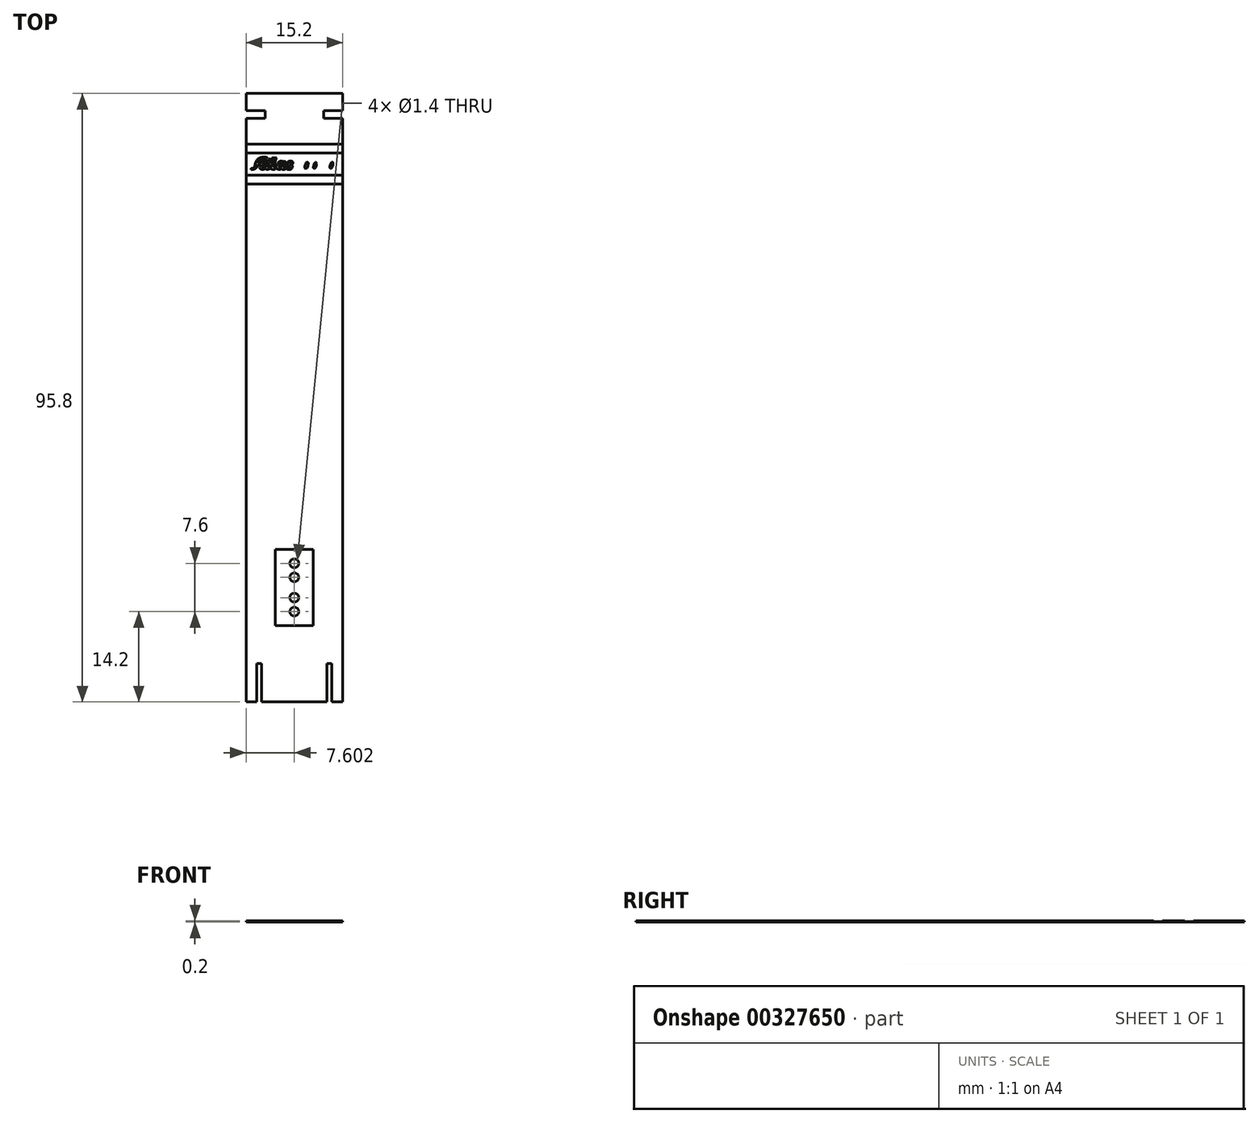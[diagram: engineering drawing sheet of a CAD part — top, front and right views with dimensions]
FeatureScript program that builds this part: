
annotation { "Feature Type Name" : "Feature", "Feature Type Description" : "" }
export const myFeature = defineFeature(function(context is Context, id is Id, definition is map)
    precondition{}
    {
        {
            var Q0;
            Q0=qCreatedBy(makeId("Top.planeOp"),FACE);
            var sketch = newSketch(context, id + "F0", { "sketchPlane" : qUnion([Q0])});
            skLineSegment(sketch, "E0.bottom", {"start": v(-50.14, 64.87) * mm, "end": v(-34.94, 64.87) * mm});
            skLineSegment(sketch, "E0.top", {"start": v(-50.14, -30.93) * mm, "end": v(-34.94, -30.93) * mm});
            skLineSegment(sketch, "E0.left", {"start": v(-50.14, 64.87) * mm, "end": v(-50.14, -30.93) * mm});
            skLineSegment(sketch, "E0.right", {"start": v(-34.94, 64.87) * mm, "end": v(-34.94, -30.93) * mm});
            skSolve(sketch);
        }
        {
            var Q0;
            Q0=makeQuery(id+"F0.imprint","IMPRINT",FACE,{"disambiguationData":[TD([[makeQuery(id+"F0.imprint","IMPRINT",EDGE,{"derivedFrom":sQuery(id+"F0.wireOp",EDGE,"E0.bottom")}),-1.0]])]});
            extrude(context, id + "F1", {"entities" : qUnion([Q0]), "depth" : 0.2 * mm});
        }
        {
            var Q0;
            Q0=makeQuery(id+"F1.opExtrude","CAP_FACE",FACE,{"disambiguationData":[OSD([sQuery(id+"F0.wireOp",EDGE,"E0.bottom"),sQuery(id+"F0.wireOp",EDGE,"E0.top"),sQuery(id+"F0.wireOp",EDGE,"E0.left"),sQuery(id+"F0.wireOp",EDGE,"E0.right")])],"isStart":false});
            var sketch = newSketch(context, id + "F2", { "sketchPlane" : qUnion([Q0])});
            skLineSegment(sketch, "E1.bottom", {"start": v(-50.14, 62.17) * mm, "end": v(-47.44, 62.17) * mm});
            skLineSegment(sketch, "E1.top", {"start": v(-50.14, 60.92) * mm, "end": v(-47.44, 60.92) * mm});
            skLineSegment(sketch, "E1.left", {"start": v(-50.14, 62.17) * mm, "end": v(-50.14, 60.92) * mm});
            skLineSegment(sketch, "E1.right", {"start": v(-47.14, 61.87) * mm, "end": v(-47.14, 61.22) * mm});
            skLineSegment(sketch, "E2.bottom", {"start": v(-34.94, 62.17) * mm, "end": v(-37.64, 62.17) * mm});
            skLineSegment(sketch, "E2.top", {"start": v(-34.94, 60.92) * mm, "end": v(-37.64, 60.92) * mm});
            skLineSegment(sketch, "E2.left", {"start": v(-34.94, 62.17) * mm, "end": v(-34.94, 60.92) * mm});
            skLineSegment(sketch, "E2.right", {"start": v(-37.94, 61.87) * mm, "end": v(-37.94, 61.22) * mm});
            skPoint(sketch, "E3.visualSharp", {"position": v(-37.94, 60.92) * mm});
            skPoint(sketch, "E4.visualSharp", {"position": v(-37.94, 62.17) * mm});
            skPoint(sketch, "E5.visualSharp", {"position": v(-47.14, 60.92) * mm});
            skPoint(sketch, "E6.visualSharp", {"position": v(-47.14, 62.17) * mm});
            skLineSegment(sketch, "E7", {"start": v(-37.94, 61.22) * mm, "end": v(-37.94, 60.92) * mm});
            skLineSegment(sketch, "E8", {"start": v(-37.64, 60.92) * mm, "end": v(-37.94, 60.92) * mm});
            skLineSegment(sketch, "E9", {"start": v(-37.94, 61.87) * mm, "end": v(-37.94, 62.17) * mm});
            skLineSegment(sketch, "E10", {"start": v(-37.64, 62.17) * mm, "end": v(-37.94, 62.17) * mm});
            skLineSegment(sketch, "E11", {"start": v(-47.44, 60.92) * mm, "end": v(-47.14, 60.92) * mm});
            skLineSegment(sketch, "E12", {"start": v(-47.14, 60.92) * mm, "end": v(-47.14, 61.22) * mm});
            skLineSegment(sketch, "E13", {"start": v(-47.14, 61.87) * mm, "end": v(-47.14, 62.17) * mm});
            skLineSegment(sketch, "E14", {"start": v(-47.14, 62.17) * mm, "end": v(-47.44, 62.17) * mm});
            skSolve(sketch);
        }
        {
            var Q0;
            Q0 = qSketchRegion(id + "F2", true);
            extrude(context, id + "F3", {"entities" : qUnion([Q0]), "operationType" : NewBodyOperationType.REMOVE, "oppositeDirection" : true, "depth" : 0.2 * mm});
        }
        {
            var Q0;
            Q0=makeQuery(id+"F1.opExtrude","CAP_FACE",FACE,{"disambiguationData":[OSD([sQuery(id+"F0.wireOp",EDGE,"E0.bottom"),sQuery(id+"F0.wireOp",EDGE,"E0.top"),sQuery(id+"F0.wireOp",EDGE,"E0.left"),sQuery(id+"F0.wireOp",EDGE,"E0.right")])],"isStart":false});
            var sketch = newSketch(context, id + "F4", { "sketchPlane" : qUnion([Q0])});
            skLineSegment(sketch, "E15", {"start": v(-48.26, 53.74) * mm, "end": v(-47.84, 53.74) * mm});
            skLineSegment(sketch, "E16", {"start": v(-47.84, 53.74) * mm, "end": v(-47.98, 53.3) * mm});
            skFitSpline(sketch, "E17", {"points": [v(-47.98, 53.3) * mm, v(-47.98, 53.14) * mm, v(-47.95, 53.02) * mm, v(-47.9, 52.98) * mm, v(-47.83, 52.94) * mm, v(-47.76, 52.92) * mm, v(-47.67, 52.9) * mm, v(-47.54, 52.88) * mm, v(-47.42, 52.9) * mm, v(-47.34, 52.94) * mm, v(-47.26, 52.97) * mm, v(-47.2, 53.02) * mm, v(-47.13, 53.08) * mm, v(-47.1, 53.12) * mm, v(-47.06, 53.12) * mm, v(-47.05, 53.07) * mm, v(-47, 52.97) * mm, v(-46.96, 52.94) * mm, v(-46.9, 52.9) * mm, v(-46.79, 52.88) * mm, v(-46.69, 52.88) * mm, v(-46.63, 52.9) * mm, v(-46.53, 52.93) * mm, v(-46.43, 52.98) * mm, v(-46.34, 53.03) * mm, v(-46.29, 53.06) * mm, v(-46.27, 53.1) * mm, v(-46.23, 53.1) * mm, v(-46.19, 53.13) * mm, v(-46.16, 53.06) * mm, v(-46.15, 53) * mm, v(-46.11, 52.95) * mm, v(-46.08, 52.92) * mm, v(-46, 52.9) * mm, v(-45.94, 52.87) * mm, v(-45.87, 52.89) * mm, v(-45.77, 52.89) * mm, v(-45.73, 52.91) * mm, v(-45.66, 52.93) * mm, v(-45.62, 52.95) * mm, v(-45.6, 52.97) * mm, v(-45.56, 53) * mm, v(-45.5, 53.03) * mm, v(-45.46, 53.09) * mm, v(-45.4, 53.13) * mm, v(-45.4, 53.18) * mm, v(-45.35, 53.2) * mm, v(-45.31, 53.2) * mm, v(-45.32, 53.15) * mm, v(-45.3, 53.1) * mm, v(-45.3, 53.08) * mm, v(-45.26, 53.04) * mm, v(-45.2, 52.98) * mm, v(-45.18, 52.95) * mm, v(-45.13, 52.91) * mm, v(-45.04, 52.88) * mm, v(-44.97, 52.87) * mm], "startDerivative": vector(-0.3, -5.65) * mm, "endDerivative": vector(3.86, 0.76) * mm});
            skFitSpline(sketch, "E18", {"points": [v(-44.97, 52.87) * mm, v(-44.9, 52.87) * mm, v(-44.85, 52.89) * mm, v(-44.81, 52.9) * mm, v(-44.77, 52.9) * mm, v(-44.73, 52.91) * mm, v(-44.72, 52.93) * mm, v(-44.68, 52.95) * mm, v(-44.67, 52.96) * mm, v(-44.64, 52.98) * mm, v(-44.6, 53) * mm, v(-44.6, 53.02) * mm, v(-44.57, 53.04) * mm, v(-44.55, 53.05) * mm, v(-44.53, 53.03) * mm, v(-44.5, 53) * mm, v(-44.48, 52.97) * mm, v(-44.46, 52.94) * mm, v(-44.44, 52.92) * mm, v(-44.42, 52.91) * mm, v(-44.4, 52.9) * mm, v(-44.36, 52.9) * mm, v(-44.33, 52.9) * mm, v(-44.28, 52.9) * mm, v(-44.24, 52.9) * mm, v(-44.21, 52.9) * mm, v(-44.18, 52.9) * mm, v(-44.16, 52.9) * mm, v(-44.12, 52.91) * mm, v(-44.08, 52.93) * mm, v(-44.03, 52.95) * mm, v(-44.02, 52.97) * mm, v(-44, 52.98) * mm, v(-43.97, 53) * mm, v(-43.94, 53.02) * mm, v(-43.92, 53.03) * mm, v(-43.89, 53.06) * mm, v(-43.87, 53.08) * mm, v(-43.85, 53.1) * mm, v(-43.83, 53.07) * mm, v(-43.81, 53.05) * mm, v(-43.78, 53) * mm, v(-43.76, 53) * mm, v(-43.75, 52.98) * mm, v(-43.72, 52.95) * mm, v(-43.7, 52.94) * mm, v(-43.67, 52.92) * mm, v(-43.65, 52.91) * mm, v(-43.64, 52.9) * mm, v(-43.59, 52.89) * mm, v(-43.55, 52.87) * mm, v(-43.53, 52.87) * mm, v(-43.5, 52.87) * mm, v(-43.47, 52.87) * mm, v(-43.43, 52.87) * mm, v(-43.39, 52.87) * mm, v(-43.35, 52.87) * mm, v(-43.3, 52.87) * mm, v(-43.25, 52.87) * mm, v(-43.22, 52.89) * mm, v(-43.2, 52.9) * mm, v(-43.15, 52.92) * mm, v(-43.1, 52.94) * mm, v(-43.07, 52.96) * mm, v(-43.05, 52.97) * mm, v(-43, 53) * mm, v(-42.97, 53.02) * mm, v(-42.94, 53.06) * mm, v(-42.9, 53.1) * mm, v(-42.9, 53.1) * mm, v(-42.87, 53.16) * mm, v(-42.85, 53.19) * mm], "startDerivative": vector(3.83, -0.43) * mm, "endDerivative": vector(1.39, 4.88) * mm});
            skFitSpline(sketch, "E19", {"points": [v(-42.85, 53.19) * mm, v(-42.84, 53.23) * mm, v(-42.83, 53.27) * mm, v(-42.82, 53.3) * mm, v(-42.83, 53.33) * mm, v(-42.83, 53.36) * mm, v(-42.83, 53.4) * mm, v(-42.83, 53.42) * mm, v(-42.85, 53.45) * mm, v(-42.85, 53.46) * mm, v(-42.86, 53.5) * mm, v(-42.89, 53.52) * mm, v(-42.92, 53.55) * mm, v(-42.96, 53.59) * mm, v(-43, 53.61) * mm, v(-43.02, 53.62) * mm, v(-43.05, 53.64) * mm, v(-43.08, 53.66) * mm, v(-43.12, 53.68) * mm, v(-43.14, 53.7) * mm, v(-43.15, 53.71) * mm, v(-43.2, 53.75) * mm, v(-43.2, 53.76) * mm, v(-43.22, 53.78) * mm, v(-43.24, 53.82) * mm, v(-43.25, 53.85) * mm, v(-43.26, 53.87) * mm, v(-43.27, 53.9) * mm, v(-43.27, 53.94) * mm, v(-43.26, 53.96) * mm, v(-43.25, 53.98) * mm, v(-43.23, 54) * mm, v(-43.21, 54.01) * mm, v(-43.2, 54.03) * mm, v(-43.17, 54.03) * mm, v(-43.15, 54.04) * mm, v(-43.13, 54.04) * mm, v(-43.1, 54.04) * mm, v(-43.08, 54.04) * mm, v(-43.07, 54.02) * mm, v(-43.07, 54) * mm, v(-43.07, 53.99) * mm, v(-43.07, 53.97) * mm, v(-43.07, 53.96) * mm, v(-43.08, 53.95) * mm, v(-43.08, 53.92) * mm, v(-43.08, 53.9) * mm, v(-43.08, 53.87) * mm, v(-43.08, 53.86) * mm, v(-43.07, 53.85) * mm, v(-43.06, 53.82) * mm, v(-43.05, 53.81) * mm, v(-43.03, 53.8) * mm, v(-43.02, 53.78) * mm, v(-43, 53.78) * mm, v(-43, 53.77) * mm, v(-42.97, 53.75) * mm, v(-42.96, 53.75) * mm, v(-42.93, 53.75) * mm, v(-42.9, 53.74) * mm, v(-42.85, 53.75) * mm, v(-42.81, 53.77) * mm, v(-42.8, 53.78) * mm, v(-42.79, 53.79) * mm, v(-42.78, 53.8) * mm, v(-42.76, 53.82) * mm, v(-42.75, 53.83) * mm, v(-42.75, 53.86) * mm, v(-42.75, 53.88) * mm], "startDerivative": vector(0.54, 2.4) * mm, "endDerivative": vector(0.03, 1.76) * mm});
            skFitSpline(sketch, "E20", {"points": [v(-42.75, 53.88) * mm, v(-42.74, 53.91) * mm, v(-42.74, 53.92) * mm, v(-42.74, 53.95) * mm, v(-42.75, 53.96) * mm, v(-42.75, 53.99) * mm, v(-42.76, 54) * mm, v(-42.76, 54.02) * mm, v(-42.77, 54.03) * mm, v(-42.77, 54.04) * mm, v(-42.78, 54.06) * mm, v(-42.8, 54.08) * mm, v(-42.8, 54.08) * mm, v(-42.8, 54.1) * mm, v(-42.81, 54.1) * mm, v(-42.81, 54.11) * mm, v(-42.83, 54.12) * mm, v(-42.84, 54.13) * mm, v(-42.85, 54.14) * mm, v(-42.86, 54.15) * mm, v(-42.87, 54.15) * mm], "startDerivative": vector(0.19, 0.47) * mm, "endDerivative": vector(-0.08, 0.05) * mm});
            skFitSpline(sketch, "E21", {"points": [v(-42.87, 54.15) * mm, v(-42.9, 54.17) * mm, v(-42.91, 54.18) * mm, v(-42.95, 54.19) * mm, v(-42.97, 54.2) * mm, v(-42.98, 54.2) * mm, v(-43.02, 54.21) * mm, v(-43.05, 54.22) * mm, v(-43.1, 54.22) * mm, v(-43.17, 54.22) * mm, v(-43.2, 54.22) * mm, v(-43.21, 54.22) * mm, v(-43.23, 54.22) * mm, v(-43.26, 54.22) * mm, v(-43.3, 54.22) * mm, v(-43.31, 54.21) * mm, v(-43.34, 54.21) * mm, v(-43.37, 54.2) * mm, v(-43.39, 54.2) * mm, v(-43.4, 54.18) * mm, v(-43.43, 54.17) * mm, v(-43.45, 54.16) * mm, v(-43.53, 54.1) * mm, v(-43.56, 54.08) * mm, v(-43.58, 54.06) * mm, v(-43.59, 54.05) * mm, v(-43.6, 54.03) * mm, v(-43.63, 54) * mm, v(-43.64, 53.97) * mm, v(-43.65, 53.93) * mm, v(-43.66, 53.91) * mm, v(-43.68, 53.87) * mm, v(-43.68, 53.83) * mm, v(-43.68, 53.8) * mm, v(-43.67, 53.76) * mm, v(-43.67, 53.72) * mm, v(-43.67, 53.7) * mm, v(-43.66, 53.67) * mm, v(-43.65, 53.64) * mm, v(-43.62, 53.62) * mm, v(-43.6, 53.6) * mm, v(-43.58, 53.57) * mm, v(-43.56, 53.55) * mm, v(-43.53, 53.54) * mm, v(-43.5, 53.52) * mm, v(-43.48, 53.5) * mm, v(-43.46, 53.48) * mm, v(-43.42, 53.45) * mm, v(-43.4, 53.43) * mm, v(-43.35, 53.4) * mm, v(-43.32, 53.38) * mm, v(-43.29, 53.35) * mm, v(-43.27, 53.33) * mm, v(-43.25, 53.29) * mm, v(-43.23, 53.24) * mm, v(-43.23, 53.2) * mm, v(-43.24, 53.17) * mm, v(-43.27, 53.12) * mm, v(-43.3, 53.1) * mm, v(-43.34, 53.07) * mm, v(-43.43, 53.05) * mm, v(-43.46, 53.05) * mm, v(-43.48, 53.05) * mm, v(-43.5, 53.05) * mm, v(-43.53, 53.06) * mm, v(-43.55, 53.06) * mm, v(-43.56, 53.06) * mm, v(-43.6, 53.07) * mm, v(-43.61, 53.1) * mm, v(-43.62, 53.1) * mm, v(-43.64, 53.13) * mm, v(-43.65, 53.15) * mm, v(-43.65, 53.16) * mm, v(-43.66, 53.2) * mm, v(-43.64, 53.2) * mm, v(-43.6, 53.2) * mm, v(-43.59, 53.22) * mm, v(-43.58, 53.23) * mm, v(-43.56, 53.25) * mm, v(-43.56, 53.26) * mm, v(-43.56, 53.27) * mm, v(-43.56, 53.3) * mm, v(-43.56, 53.31) * mm, v(-43.56, 53.34) * mm, v(-43.56, 53.38) * mm, v(-43.56, 53.4) * mm, v(-43.57, 53.42) * mm, v(-43.6, 53.43) * mm, v(-43.6, 53.45) * mm, v(-43.63, 53.46) * mm, v(-43.7, 53.48) * mm, v(-43.73, 53.49) * mm], "startDerivative": vector(-2.33, 2.26) * mm, "endDerivative": vector(-4.26, -1.5) * mm});
            skFitSpline(sketch, "E22", {"points": [v(-43.73, 53.49) * mm, v(-43.77, 53.49) * mm, v(-43.79, 53.47) * mm, v(-43.81, 53.45) * mm, v(-43.83, 53.44) * mm, v(-43.85, 53.43) * mm, v(-43.86, 53.41) * mm, v(-43.87, 53.4) * mm, v(-43.87, 53.39) * mm, v(-43.88, 53.37) * mm, v(-43.88, 53.35) * mm, v(-43.88, 53.33) * mm, v(-43.88, 53.31) * mm, v(-43.88, 53.3) * mm, v(-43.88, 53.28) * mm, v(-43.89, 53.26) * mm, v(-43.9, 53.25) * mm, v(-43.92, 53.23) * mm, v(-43.94, 53.22) * mm, v(-43.95, 53.2) * mm, v(-43.97, 53.18) * mm, v(-43.98, 53.18) * mm, v(-44, 53.18) * mm, v(-44.04, 53.18) * mm, v(-44.08, 53.18) * mm, v(-44.1, 53.19) * mm, v(-44.12, 53.2) * mm, v(-44.13, 53.2) * mm, v(-44.14, 53.23) * mm, v(-44.14, 53.25) * mm, v(-44.14, 53.27) * mm, v(-44.13, 53.31) * mm, v(-44.13, 53.34) * mm, v(-44.13, 53.36) * mm, v(-44.12, 53.38) * mm, v(-44.12, 53.4) * mm, v(-44.11, 53.42) * mm, v(-44.1, 53.47) * mm, v(-44.1, 53.5) * mm, v(-44.1, 53.52) * mm, v(-44.09, 53.54) * mm, v(-44.08, 53.56) * mm, v(-44.08, 53.58) * mm, v(-44.07, 53.6) * mm, v(-44.06, 53.62) * mm, v(-44.06, 53.66) * mm, v(-44.05, 53.68) * mm, v(-44.05, 53.71) * mm, v(-44.04, 53.74) * mm, v(-44.04, 53.75) * mm, v(-44.02, 53.87) * mm, v(-44, 53.97) * mm, v(-43.98, 54.01) * mm, v(-43.96, 54.05) * mm, v(-43.96, 54.08) * mm, v(-43.94, 54.1) * mm, v(-43.94, 54.15) * mm, v(-43.94, 54.17) * mm, v(-43.94, 54.18) * mm, v(-43.96, 54.17) * mm, v(-44.04, 54.17) * mm, v(-44.09, 54.18) * mm, v(-44.12, 54.18) * mm, v(-44.16, 54.17) * mm, v(-44.2, 54.18) * mm, v(-44.26, 54.18) * mm, v(-44.3, 54.18) * mm, v(-44.31, 54.12) * mm, v(-44.33, 54.1) * mm, v(-44.38, 54.11) * mm, v(-44.4, 54.13) * mm, v(-44.4, 54.15) * mm, v(-44.44, 54.18) * mm, v(-44.46, 54.18) * mm, v(-44.5, 54.2) * mm, v(-44.53, 54.2) * mm, v(-44.59, 54.2) * mm, v(-44.64, 54.21) * mm, v(-44.7, 54.21) * mm, v(-44.72, 54.21) * mm, v(-44.76, 54.2) * mm, v(-44.82, 54.2) * mm, v(-44.82, 54.17) * mm, v(-44.85, 54.16) * mm, v(-44.88, 54.14) * mm, v(-44.9, 54.12) * mm, v(-44.94, 54.1) * mm, v(-44.97, 54.08) * mm, v(-44.99, 54.06) * mm, v(-45, 54.04) * mm, v(-45.02, 54.01) * mm], "startDerivative": vector(-3.3, 0.4) * mm, "endDerivative": vector(-1.45, -2.51) * mm});
            skFitSpline(sketch, "E23", {"points": [v(-45.02, 54.01) * mm, v(-45.08, 53.94) * mm, v(-45.13, 53.87) * mm, v(-45.16, 53.83) * mm, v(-45.22, 53.73) * mm, v(-45.26, 53.67) * mm, v(-45.28, 53.64) * mm, v(-45.3, 53.59) * mm, v(-45.32, 53.56) * mm, v(-45.35, 53.52) * mm, v(-45.36, 53.49) * mm, v(-45.38, 53.45) * mm, v(-45.4, 53.43) * mm, v(-45.44, 53.37) * mm, v(-45.46, 53.34) * mm, v(-45.47, 53.33) * mm, v(-45.5, 53.3) * mm, v(-45.51, 53.29) * mm, v(-45.53, 53.26) * mm, v(-45.55, 53.23) * mm, v(-45.57, 53.22) * mm, v(-45.58, 53.2) * mm, v(-45.6, 53.18) * mm, v(-45.62, 53.17) * mm, v(-45.66, 53.17) * mm, v(-45.7, 53.18) * mm, v(-45.72, 53.2) * mm, v(-45.73, 53.2) * mm, v(-45.74, 53.2) * mm, v(-45.75, 53.24) * mm, v(-45.75, 53.26) * mm, v(-45.73, 53.3) * mm, v(-45.72, 53.33) * mm, v(-45.71, 53.36) * mm, v(-45.7, 53.39) * mm, v(-45.7, 53.4) * mm, v(-45.7, 53.43) * mm, v(-45.69, 53.45) * mm, v(-45.68, 53.49) * mm, v(-45.67, 53.53) * mm, v(-45.65, 53.6) * mm, v(-45.64, 53.62) * mm, v(-45.64, 53.66) * mm, v(-45.62, 53.7) * mm, v(-45.62, 53.74) * mm, v(-45.61, 53.77) * mm, v(-45.6, 53.83) * mm, v(-45.59, 53.9) * mm, v(-45.57, 53.96) * mm], "startDerivative": vector(-2.11, -2.16) * mm, "endDerivative": vector(0.65, 1.77) * mm});
            skFitSpline(sketch, "E24", {"points": [v(-45.57, 53.96) * mm, v(-45.55, 54.05) * mm, v(-45.52, 54.15) * mm, v(-45.5, 54.22) * mm, v(-45.47, 54.4) * mm, v(-45.42, 54.57) * mm, v(-45.38, 54.68) * mm, v(-45.38, 54.74) * mm, v(-45.52, 54.75) * mm, v(-45.67, 54.76) * mm, v(-45.83, 54.75) * mm, v(-45.95, 54.75) * mm, v(-46, 54.75) * mm, v(-46.05, 54.74) * mm, v(-46.07, 54.69) * mm, v(-46.06, 54.63) * mm, v(-46.06, 54.6) * mm, v(-45.97, 54.6) * mm, v(-45.9, 54.6) * mm, v(-45.86, 54.6) * mm, v(-45.84, 54.57) * mm, v(-45.85, 54.51) * mm, v(-45.86, 54.46) * mm], "startDerivative": vector(0.55, 1.72) * mm, "endDerivative": vector(-0.56, -1.4) * mm});
            skFitSpline(sketch, "E25", {"points": [v(-45.86, 54.46) * mm, v(-45.87, 54.39) * mm, v(-45.9, 54.29) * mm, v(-45.92, 54.16) * mm, v(-45.93, 54.04) * mm, v(-45.95, 53.97) * mm, v(-45.98, 53.88) * mm, v(-46, 53.77) * mm, v(-46.02, 53.72) * mm, v(-46.03, 53.66) * mm, v(-46.06, 53.6) * mm, v(-46.08, 53.56) * mm, v(-46.09, 53.5) * mm, v(-46.12, 53.47) * mm, v(-46.13, 53.44) * mm, v(-46.16, 53.4) * mm, v(-46.17, 53.38) * mm, v(-46.2, 53.35) * mm, v(-46.22, 53.33) * mm, v(-46.26, 53.29) * mm, v(-46.28, 53.27) * mm, v(-46.32, 53.25) * mm, v(-46.36, 53.21) * mm, v(-46.4, 53.2) * mm, v(-46.44, 53.18) * mm, v(-46.46, 53.16) * mm, v(-46.48, 53.16) * mm, v(-46.52, 53.15) * mm, v(-46.55, 53.15) * mm, v(-46.58, 53.16) * mm, v(-46.62, 53.18) * mm, v(-46.64, 53.2) * mm, v(-46.65, 53.23) * mm, v(-46.65, 53.29) * mm, v(-46.65, 53.35) * mm, v(-46.64, 53.38) * mm, v(-46.63, 53.4) * mm, v(-46.62, 53.44) * mm, v(-46.6, 53.46) * mm, v(-46.6, 53.49) * mm, v(-46.59, 53.51) * mm, v(-46.58, 53.55) * mm, v(-46.58, 53.59) * mm, v(-46.56, 53.63) * mm, v(-46.56, 53.68) * mm, v(-46.55, 53.7) * mm, v(-46.55, 53.75) * mm, v(-46.53, 53.79) * mm, v(-46.53, 53.83) * mm, v(-46.52, 53.86) * mm, v(-46.51, 53.9) * mm, v(-46.5, 53.9) * mm, v(-46.5, 53.95) * mm, v(-46.49, 53.98) * mm, v(-46.48, 54.02) * mm, v(-46.42, 54.03) * mm, v(-46.38, 54.03) * mm, v(-46.34, 54.03) * mm, v(-46.31, 54.03) * mm, v(-46.27, 54.02) * mm, v(-46.24, 54.02) * mm, v(-46.2, 54.03) * mm, v(-46.2, 54.03) * mm, v(-46.18, 54.03) * mm, v(-46.18, 54.07) * mm, v(-46.18, 54.1) * mm, v(-46.17, 54.15) * mm, v(-46.17, 54.17) * mm, v(-46.17, 54.18) * mm, v(-46.21, 54.18) * mm, v(-46.26, 54.18) * mm, v(-46.33, 54.18) * mm, v(-46.4, 54.19) * mm, v(-46.44, 54.18) * mm, v(-46.43, 54.24) * mm, v(-46.4, 54.3) * mm, v(-46.38, 54.39) * mm, v(-46.38, 54.46) * mm, v(-46.36, 54.52) * mm, v(-46.36, 54.55) * mm, v(-46.4, 54.58) * mm, v(-46.46, 54.58) * mm, v(-46.5, 54.57) * mm, v(-46.52, 54.54) * mm, v(-46.54, 54.5) * mm, v(-46.55, 54.46) * mm, v(-46.57, 54.43) * mm, v(-46.6, 54.38) * mm], "startDerivative": vector(-1.08, -4.44) * mm, "endDerivative": vector(-2.08, -3.86) * mm});
            skFitSpline(sketch, "E26", {"points": [v(-46.6, 54.38) * mm, v(-46.62, 54.34) * mm, v(-46.65, 54.33) * mm, v(-46.68, 54.3) * mm, v(-46.7, 54.27) * mm, v(-46.72, 54.25) * mm, v(-46.74, 54.23) * mm, v(-46.76, 54.22) * mm, v(-46.8, 54.2) * mm, v(-46.84, 54.2) * mm, v(-46.86, 54.2) * mm, v(-46.91, 54.2) * mm, v(-46.95, 54.2) * mm, v(-47, 54.2) * mm, v(-47.04, 54.2) * mm, v(-47.07, 54.2) * mm, v(-47.08, 54.15) * mm, v(-47.08, 54.08) * mm, v(-47.09, 54.05) * mm, v(-47.08, 54.03) * mm, v(-47.05, 54.04) * mm, v(-47.01, 54.03) * mm, v(-46.97, 54.02) * mm, v(-46.94, 54.02) * mm, v(-46.91, 54.02) * mm, v(-46.89, 54.02) * mm, v(-46.87, 54) * mm, v(-46.88, 53.97) * mm, v(-46.9, 53.95) * mm, v(-46.91, 53.91) * mm, v(-46.91, 53.88) * mm, v(-46.92, 53.85) * mm, v(-46.93, 53.83) * mm, v(-46.94, 53.8) * mm, v(-46.96, 53.73) * mm, v(-46.97, 53.67) * mm, v(-47, 53.63) * mm, v(-47, 53.59) * mm, v(-47.02, 53.53) * mm, v(-47.04, 53.49) * mm, v(-47.06, 53.46) * mm, v(-47.08, 53.4) * mm, v(-47.12, 53.34) * mm, v(-47.16, 53.29) * mm, v(-47.18, 53.25) * mm, v(-47.22, 53.2) * mm, v(-47.25, 53.18) * mm, v(-47.28, 53.16) * mm, v(-47.32, 53.14) * mm, v(-47.34, 53.13) * mm, v(-47.39, 53.12) * mm, v(-47.43, 53.12) * mm, v(-47.48, 53.13) * mm, v(-47.53, 53.15) * mm, v(-47.53, 53.16) * mm, v(-47.54, 53.2) * mm, v(-47.54, 53.23) * mm, v(-47.53, 53.28) * mm, v(-47.52, 53.31) * mm, v(-47.51, 53.37) * mm, v(-47.5, 53.43) * mm, v(-47.49, 53.48) * mm, v(-47.47, 53.55) * mm, v(-47.45, 53.63) * mm, v(-47.43, 53.7) * mm], "startDerivative": vector(-1.57, -2.6) * mm, "endDerivative": vector(0.74, 3.03) * mm});
            skFitSpline(sketch, "E27", {"points": [v(-47.43, 53.7) * mm, v(-47.4, 53.8) * mm, v(-47.38, 53.89) * mm, v(-47.35, 53.97) * mm, v(-47.33, 54.04) * mm, v(-47.3, 54.11) * mm, v(-47.28, 54.2) * mm, v(-47.27, 54.29) * mm, v(-47.25, 54.37) * mm, v(-47.23, 54.47) * mm, v(-47.21, 54.52) * mm, v(-47.2, 54.56) * mm, v(-47.18, 54.62) * mm, v(-47.18, 54.66) * mm, v(-47.17, 54.68) * mm, v(-47.07, 54.68) * mm, v(-46.98, 54.67) * mm, v(-46.91, 54.68) * mm, v(-46.9, 54.68) * mm, v(-46.89, 54.73) * mm, v(-46.89, 54.77) * mm, v(-46.9, 54.8) * mm, v(-46.9, 54.82) * mm, v(-46.9, 54.83) * mm, v(-47.01, 54.84) * mm, v(-47.1, 54.85) * mm, v(-47.19, 54.85) * mm, v(-47.3, 54.85) * mm, v(-47.4, 54.85) * mm, v(-47.43, 54.84) * mm, v(-47.48, 54.84) * mm, v(-47.53, 54.83) * mm, v(-47.6, 54.83) * mm, v(-47.64, 54.82) * mm, v(-47.7, 54.81) * mm, v(-47.73, 54.81) * mm, v(-47.8, 54.8) * mm, v(-47.86, 54.78) * mm, v(-47.91, 54.76) * mm, v(-47.94, 54.76) * mm, v(-48, 54.73) * mm, v(-48.06, 54.69) * mm, v(-48.14, 54.64) * mm, v(-48.17, 54.62) * mm, v(-48.2, 54.6) * mm, v(-48.24, 54.56) * mm, v(-48.32, 54.5) * mm, v(-48.35, 54.48) * mm, v(-48.38, 54.45) * mm, v(-48.4, 54.42) * mm, v(-48.43, 54.38) * mm, v(-48.45, 54.34) * mm, v(-48.5, 54.26) * mm, v(-48.52, 54.22) * mm, v(-48.54, 54.16) * mm, v(-48.57, 54.08) * mm, v(-48.6, 54.02) * mm, v(-48.61, 53.96) * mm, v(-48.65, 53.86) * mm, v(-48.69, 53.8) * mm, v(-48.71, 53.73) * mm], "startDerivative": vector(1.47, 4.58) * mm, "endDerivative": vector(0.15, -3.5) * mm});
            skFitSpline(sketch, "E28", {"points": [v(-48.71, 53.73) * mm, v(-48.71, 53.64) * mm, v(-48.71, 53.61) * mm, v(-48.74, 53.55) * mm, v(-48.75, 53.5) * mm, v(-48.76, 53.46) * mm, v(-48.76, 53.4) * mm, v(-48.79, 53.36) * mm, v(-48.8, 53.33) * mm, v(-48.8, 53.28) * mm, v(-48.82, 53.25) * mm, v(-48.84, 53.22) * mm, v(-48.86, 53.2) * mm, v(-48.9, 53.16) * mm, v(-48.92, 53.13) * mm, v(-48.94, 53.11) * mm, v(-48.96, 53.1) * mm, v(-49, 53.07) * mm, v(-49.03, 53.06) * mm, v(-49.05, 53.05) * mm, v(-49.08, 53.04) * mm, v(-49.1, 53.04) * mm, v(-49.13, 53.04) * mm, v(-49.18, 53.05) * mm, v(-49.23, 53.05) * mm, v(-49.25, 53.05) * mm, v(-49.26, 53.06) * mm, v(-49.3, 53.07) * mm, v(-49.31, 53.08) * mm, v(-49.34, 53.08) * mm, v(-49.34, 53.08) * mm, v(-49.34, 53.05) * mm, v(-49.34, 53.02) * mm, v(-49.34, 52.99) * mm, v(-49.34, 52.96) * mm, v(-49.34, 52.92) * mm, v(-49.34, 52.91) * mm, v(-49.34, 52.89) * mm, v(-49.34, 52.89) * mm, v(-49.27, 52.88) * mm, v(-49.23, 52.88) * mm, v(-49.21, 52.88) * mm, v(-49.17, 52.88) * mm, v(-49.12, 52.88) * mm, v(-49.05, 52.9) * mm, v(-49.01, 52.9) * mm, v(-48.95, 52.9) * mm, v(-48.88, 52.92) * mm, v(-48.84, 52.94) * mm, v(-48.8, 52.95) * mm, v(-48.76, 52.97) * mm, v(-48.73, 53) * mm, v(-48.71, 53) * mm, v(-48.67, 53.04) * mm, v(-48.65, 53.05) * mm, v(-48.63, 53.06) * mm, v(-48.61, 53.08) * mm, v(-48.6, 53.1) * mm, v(-48.56, 53.12) * mm, v(-48.54, 53.14) * mm, v(-48.5, 53.17) * mm, v(-48.47, 53.21) * mm, v(-48.43, 53.27) * mm, v(-48.41, 53.3) * mm, v(-48.4, 53.33) * mm, v(-48.38, 53.37) * mm, v(-48.37, 53.39) * mm, v(-48.35, 53.41) * mm, v(-48.35, 53.44) * mm, v(-48.33, 53.47) * mm, v(-48.32, 53.5) * mm, v(-48.31, 53.54) * mm, v(-48.3, 53.57) * mm, v(-48.3, 53.6) * mm, v(-48.28, 53.64) * mm, v(-48.27, 53.68) * mm, v(-48.27, 53.73) * mm, v(-48.26, 53.74) * mm], "startDerivative": vector(-0.25, -4.76) * mm, "endDerivative": vector(1.5, 0.83) * mm});
            skFitSpline(sketch, "E29", {"points": [v(-48.2, 53.9) * mm, v(-47.82, 53.89) * mm, v(-47.79, 53.9) * mm, v(-47.77, 53.94) * mm, v(-47.77, 53.97) * mm, v(-47.76, 54) * mm, v(-47.75, 54.04) * mm, v(-47.73, 54.15) * mm, v(-47.71, 54.22) * mm, v(-47.7, 54.24) * mm, v(-47.68, 54.28) * mm, v(-47.67, 54.32) * mm, v(-47.65, 54.35) * mm, v(-47.64, 54.4) * mm, v(-47.63, 54.44) * mm, v(-47.6, 54.5) * mm, v(-47.6, 54.54) * mm, v(-47.6, 54.57) * mm, v(-47.57, 54.62) * mm, v(-47.57, 54.64) * mm, v(-47.57, 54.68) * mm, v(-47.6, 54.68) * mm, v(-47.63, 54.68) * mm, v(-47.67, 54.68) * mm, v(-47.7, 54.68) * mm, v(-47.76, 54.66) * mm, v(-47.78, 54.65) * mm, v(-47.8, 54.63) * mm, v(-47.85, 54.6) * mm, v(-47.88, 54.58) * mm, v(-47.92, 54.55) * mm, v(-47.93, 54.54) * mm, v(-47.96, 54.5) * mm, v(-47.99, 54.46) * mm, v(-48.02, 54.43) * mm, v(-48.03, 54.4) * mm, v(-48.05, 54.38) * mm, v(-48.06, 54.34) * mm, v(-48.08, 54.32) * mm, v(-48.09, 54.3) * mm, v(-48.11, 54.26) * mm, v(-48.12, 54.22) * mm, v(-48.15, 54.17) * mm, v(-48.17, 54.14) * mm, v(-48.17, 54.1) * mm, v(-48.19, 54.05) * mm, v(-48.19, 54) * mm, v(-48.2, 53.97) * mm, v(-48.2, 53.95) * mm, v(-48.2, 53.9) * mm]});
            skFitSpline(sketch, "E30", {"points": [v(-44.56, 54.02) * mm, v(-44.62, 54.01) * mm, v(-44.67, 54) * mm, v(-44.7, 53.98) * mm, v(-44.71, 53.96) * mm, v(-44.73, 53.93) * mm, v(-44.76, 53.9) * mm, v(-44.8, 53.85) * mm, v(-44.82, 53.82) * mm, v(-44.82, 53.79) * mm, v(-44.82, 53.76) * mm, v(-44.84, 53.73) * mm, v(-44.85, 53.68) * mm, v(-44.87, 53.63) * mm, v(-44.88, 53.58) * mm, v(-44.9, 53.54) * mm, v(-44.9, 53.52) * mm, v(-44.9, 53.48) * mm, v(-44.9, 53.44) * mm, v(-44.91, 53.4) * mm, v(-44.92, 53.37) * mm, v(-44.92, 53.34) * mm, v(-44.9, 53.3) * mm, v(-44.9, 53.26) * mm, v(-44.88, 53.23) * mm, v(-44.87, 53.2) * mm, v(-44.85, 53.2) * mm, v(-44.83, 53.17) * mm, v(-44.82, 53.16) * mm, v(-44.76, 53.16) * mm, v(-44.75, 53.16) * mm, v(-44.72, 53.16) * mm, v(-44.7, 53.16) * mm, v(-44.68, 53.16) * mm, v(-44.64, 53.17) * mm, v(-44.64, 53.18) * mm, v(-44.62, 53.22) * mm, v(-44.6, 53.25) * mm, v(-44.6, 53.3) * mm, v(-44.58, 53.32) * mm, v(-44.56, 53.35) * mm, v(-44.55, 53.38) * mm, v(-44.53, 53.4) * mm, v(-44.53, 53.46) * mm, v(-44.5, 53.47) * mm, v(-44.5, 53.5) * mm, v(-44.5, 53.52) * mm, v(-44.48, 53.54) * mm, v(-44.48, 53.58) * mm, v(-44.47, 53.62) * mm, v(-44.47, 53.65) * mm, v(-44.45, 53.7) * mm, v(-44.46, 53.73) * mm, v(-44.45, 53.74) * mm, v(-44.46, 53.8) * mm, v(-44.45, 53.83) * mm, v(-44.45, 53.87) * mm, v(-44.44, 53.9) * mm, v(-44.44, 53.92) * mm, v(-44.45, 53.94) * mm, v(-44.45, 53.98) * mm, v(-44.47, 54) * mm, v(-44.51, 54.02) * mm, v(-44.54, 54.01) * mm, v(-44.56, 54.02) * mm]});
            skLineSegment(sketch, "E31.bottom", {"start": v(-50.14, 56.87) * mm, "end": v(-34.94, 56.87) * mm});
            skLineSegment(sketch, "E31.top", {"start": v(-50.14, 55.47) * mm, "end": v(-34.94, 55.47) * mm});
            skLineSegment(sketch, "E31.left", {"start": v(-50.14, 56.87) * mm, "end": v(-50.14, 55.47) * mm});
            skLineSegment(sketch, "E31.right", {"start": v(-34.94, 56.87) * mm, "end": v(-34.94, 55.47) * mm});
            skLineSegment(sketch, "E32.bottom", {"start": v(-50.14, 50.58) * mm, "end": v(-34.94, 50.58) * mm});
            skLineSegment(sketch, "E32.top", {"start": v(-50.14, 51.98) * mm, "end": v(-34.94, 51.98) * mm});
            skLineSegment(sketch, "E32.left", {"start": v(-50.14, 50.58) * mm, "end": v(-50.14, 51.98) * mm});
            skLineSegment(sketch, "E32.right", {"start": v(-34.94, 50.58) * mm, "end": v(-34.94, 51.98) * mm});
            skFitSpline(sketch, "E33", {"points": [v(-42.2, 53) * mm, v(-42.1, 52.96) * mm, v(-42.06, 52.92) * mm, v(-41.96, 52.91) * mm, v(-41.92, 52.91) * mm, v(-41.87, 52.91) * mm, v(-41.83, 52.92) * mm, v(-41.8, 52.92) * mm, v(-41.73, 52.91) * mm, v(-41.69, 52.93) * mm, v(-41.65, 52.94) * mm, v(-41.6, 52.96) * mm, v(-41.56, 52.97) * mm, v(-41.52, 53) * mm, v(-41.5, 53.02) * mm, v(-41.44, 53.05) * mm, v(-41.42, 53.06) * mm, v(-41.4, 53.08) * mm, v(-41.37, 53.1) * mm, v(-41.34, 53.13) * mm, v(-41.31, 53.16) * mm, v(-41.28, 53.2) * mm, v(-41.26, 53.21) * mm], "startDerivative": vector(1.44, -0.61) * mm, "endDerivative": vector(0.47, 0.45) * mm});
            skFitSpline(sketch, "E34", {"points": [v(-41.26, 53.21) * mm, v(-41.24, 53.2) * mm, v(-41.24, 53.15) * mm, v(-41.23, 53.13) * mm, v(-41.21, 53.12) * mm, v(-41.2, 53.09) * mm, v(-41.18, 53.06) * mm, v(-41.17, 53.05) * mm, v(-41.13, 53.02) * mm, v(-41.12, 53) * mm, v(-41.1, 53) * mm, v(-41.08, 52.97) * mm, v(-41.06, 52.96) * mm, v(-41.05, 52.94) * mm, v(-41.02, 52.94) * mm, v(-41, 52.93) * mm, v(-40.98, 52.92) * mm, v(-40.95, 52.9) * mm], "startDerivative": vector(0.36, -0.22) * mm, "endDerivative": vector(0.8, -0.36) * mm});
            skFitSpline(sketch, "E35", {"points": [v(-40.95, 52.9) * mm, v(-40.9, 52.9) * mm, v(-40.87, 52.9) * mm, v(-40.83, 52.9) * mm, v(-40.8, 52.9) * mm, v(-40.77, 52.9) * mm, v(-40.74, 52.9) * mm, v(-40.72, 52.9) * mm, v(-40.68, 52.9) * mm, v(-40.66, 52.9) * mm, v(-40.65, 52.92) * mm, v(-40.62, 52.93) * mm, v(-40.6, 52.94) * mm, v(-40.59, 52.95) * mm, v(-40.56, 52.96) * mm, v(-40.55, 52.97) * mm, v(-40.51, 52.98) * mm, v(-40.49, 53) * mm, v(-40.45, 53.01) * mm, v(-40.42, 53.03) * mm, v(-40.4, 53.05) * mm, v(-40.38, 53.06) * mm, v(-40.35, 53.08) * mm, v(-40.33, 53.09) * mm, v(-40.3, 53.1) * mm, v(-40.28, 53.13) * mm, v(-40.24, 53.15) * mm, v(-40.23, 53.17) * mm, v(-40.2, 53.2) * mm, v(-40.18, 53.22) * mm, v(-40.16, 53.23) * mm, v(-40.14, 53.26) * mm, v(-40.09, 53.3) * mm, v(-40.07, 53.31) * mm, v(-40.03, 53.36) * mm, v(-40.01, 53.38) * mm, v(-40, 53.4) * mm, v(-39.96, 53.42) * mm, v(-39.94, 53.45) * mm, v(-39.92, 53.45) * mm, v(-39.9, 53.46) * mm, v(-39.9, 53.44) * mm, v(-39.9, 53.43) * mm, v(-39.9, 53.4) * mm, v(-39.9, 53.37) * mm, v(-39.9, 53.35) * mm, v(-39.9, 53.32) * mm, v(-39.91, 53.3) * mm, v(-39.92, 53.27) * mm, v(-39.93, 53.24) * mm, v(-39.93, 53.2) * mm, v(-39.94, 53.18) * mm, v(-39.95, 53.14) * mm, v(-39.97, 53.1) * mm, v(-39.98, 53.07) * mm, v(-39.98, 53.02) * mm, v(-40, 53) * mm, v(-40, 52.94) * mm, v(-40, 52.9) * mm, v(-40.02, 52.88) * mm, v(-40.02, 52.86) * mm, v(-40.03, 52.83) * mm, v(-40.04, 52.8) * mm, v(-40.03, 52.78) * mm], "startDerivative": vector(2.29, -0.51) * mm, "endDerivative": vector(0.2, -1.58) * mm});
            skFitSpline(sketch, "E36", {"points": [v(-40.03, 52.78) * mm, v(-40.05, 52.74) * mm, v(-40.05, 52.72) * mm, v(-40.06, 52.7) * mm, v(-40.06, 52.68) * mm, v(-40.07, 52.65) * mm, v(-40.07, 52.62) * mm, v(-40.08, 52.6) * mm, v(-40.09, 52.58) * mm, v(-40.1, 52.54) * mm, v(-40.1, 52.53) * mm, v(-40.1, 52.49) * mm, v(-40.07, 52.48) * mm, v(-40.03, 52.48) * mm, v(-40, 52.48) * mm, v(-39.96, 52.48) * mm, v(-39.9, 52.47) * mm, v(-39.87, 52.47) * mm, v(-39.84, 52.48) * mm, v(-39.82, 52.47) * mm, v(-39.78, 52.47) * mm, v(-39.77, 52.47) * mm, v(-39.76, 52.47) * mm, v(-39.74, 52.48) * mm, v(-39.73, 52.5) * mm, v(-39.73, 52.52) * mm, v(-39.71, 52.56) * mm, v(-39.7, 52.6) * mm, v(-39.7, 52.64) * mm, v(-39.7, 52.7) * mm, v(-39.68, 52.71) * mm, v(-39.67, 52.76) * mm, v(-39.67, 52.78) * mm, v(-39.66, 52.82) * mm, v(-39.66, 52.84) * mm, v(-39.65, 52.86) * mm, v(-39.64, 52.9) * mm, v(-39.63, 52.94) * mm, v(-39.63, 52.97) * mm, v(-39.62, 52.99) * mm, v(-39.6, 53) * mm, v(-39.59, 53) * mm], "startDerivative": vector(-0.85, -1.24) * mm, "endDerivative": vector(1.57, 0.39) * mm});
            skFitSpline(sketch, "E37", {"points": [v(-39.59, 53) * mm, v(-39.57, 52.99) * mm, v(-39.55, 52.97) * mm, v(-39.54, 52.97) * mm, v(-39.52, 52.96) * mm, v(-39.51, 52.95) * mm, v(-39.5, 52.94) * mm, v(-39.5, 52.94) * mm, v(-39.48, 52.93) * mm, v(-39.47, 52.93) * mm, v(-39.46, 52.93) * mm, v(-39.46, 52.92) * mm, v(-39.45, 52.92) * mm, v(-39.43, 52.92) * mm, v(-39.41, 52.92) * mm, v(-39.4, 52.92) * mm, v(-39.36, 52.91) * mm, v(-39.33, 52.9) * mm, v(-39.3, 52.91) * mm, v(-39.27, 52.91) * mm, v(-39.22, 52.92) * mm, v(-39.2, 52.92) * mm, v(-39.18, 52.93) * mm, v(-39.14, 52.95) * mm, v(-39.12, 52.96) * mm, v(-39.1, 52.96) * mm, v(-39.06, 52.98) * mm, v(-39.02, 53) * mm, v(-39, 53) * mm, v(-38.98, 53.03) * mm, v(-38.97, 53.04) * mm, v(-38.95, 53.06) * mm, v(-38.93, 53.06) * mm, v(-38.9, 53.09) * mm], "startDerivative": vector(0.63, -0.51) * mm, "endDerivative": vector(1.06, 1.15) * mm});
            skFitSpline(sketch, "E38", {"points": [v(-38.9, 53.09) * mm, v(-38.88, 53.1) * mm, v(-38.84, 53.13) * mm, v(-38.82, 53.15) * mm, v(-38.79, 53.18) * mm, v(-38.76, 53.2) * mm, v(-38.73, 53.23) * mm, v(-38.7, 53.26) * mm, v(-38.68, 53.27) * mm, v(-38.65, 53.3) * mm, v(-38.63, 53.32) * mm, v(-38.6, 53.35) * mm, v(-38.57, 53.37) * mm, v(-38.55, 53.4) * mm, v(-38.53, 53.41) * mm], "startDerivative": vector(0.36, 0.2) * mm, "endDerivative": vector(0.33, 0.33) * mm});
            skFitSpline(sketch, "E39", {"points": [v(-38.53, 53.4) * mm, v(-38.5, 53.44) * mm, v(-38.49, 53.45) * mm, v(-38.48, 53.47) * mm, v(-38.45, 53.48) * mm, v(-38.45, 53.47) * mm, v(-38.45, 53.46) * mm, v(-38.44, 53.44) * mm, v(-38.45, 53.41) * mm, v(-38.45, 53.4) * mm, v(-38.46, 53.39) * mm, v(-38.46, 53.36) * mm, v(-38.46, 53.35) * mm, v(-38.46, 53.33) * mm, v(-38.46, 53.3) * mm, v(-38.45, 53.26) * mm, v(-38.45, 53.24) * mm, v(-38.44, 53.2) * mm, v(-38.43, 53.18) * mm, v(-38.42, 53.16) * mm, v(-38.4, 53.13) * mm, v(-38.4, 53.1) * mm, v(-38.4, 53.1) * mm, v(-38.38, 53.07) * mm, v(-38.37, 53.06) * mm, v(-38.36, 53.02) * mm, v(-38.34, 53) * mm, v(-38.33, 52.98) * mm, v(-38.3, 52.96) * mm, v(-38.28, 52.95) * mm, v(-38.26, 52.94) * mm, v(-38.24, 52.93) * mm, v(-38.21, 52.91) * mm, v(-38.17, 52.9) * mm, v(-38.16, 52.9) * mm, v(-38.13, 52.9) * mm, v(-38.1, 52.89) * mm, v(-38.06, 52.88) * mm, v(-38.05, 52.88) * mm, v(-38.02, 52.88) * mm, v(-38, 52.88) * mm, v(-37.96, 52.88) * mm, v(-37.93, 52.89) * mm, v(-37.91, 52.89) * mm, v(-37.89, 52.9) * mm, v(-37.87, 52.9) * mm, v(-37.84, 52.9) * mm, v(-37.81, 52.92) * mm, v(-37.8, 52.93) * mm, v(-37.76, 52.94) * mm, v(-37.74, 52.96) * mm, v(-37.72, 52.97) * mm, v(-37.7, 52.98) * mm, v(-37.69, 53) * mm, v(-37.66, 53) * mm, v(-37.63, 53.02) * mm], "startDerivative": vector(1.46, 1.37) * mm, "endDerivative": vector(1.1, 0.18) * mm});
            skFitSpline(sketch, "E40", {"points": [v(-37.63, 53.02) * mm, v(-37.6, 53.05) * mm, v(-37.58, 53.07) * mm, v(-37.55, 53.1) * mm], "startDerivative": vector(0.09, 0.09) * mm, "endDerivative": vector(0.06, 0.1) * mm});
            skFitSpline(sketch, "E41", {"points": [v(-37.55, 53.1) * mm, v(-37.52, 53.13) * mm, v(-37.5, 53.15) * mm, v(-37.48, 53.17) * mm, v(-37.46, 53.2) * mm, v(-37.44, 53.2) * mm, v(-37.43, 53.23) * mm, v(-37.42, 53.24) * mm, v(-37.4, 53.25) * mm, v(-37.4, 53.27) * mm, v(-37.38, 53.28) * mm, v(-37.37, 53.3) * mm, v(-37.36, 53.3) * mm, v(-37.35, 53.3) * mm, v(-37.34, 53.28) * mm, v(-37.34, 53.27) * mm, v(-37.34, 53.25) * mm, v(-37.34, 53.23) * mm, v(-37.33, 53.2) * mm, v(-37.32, 53.18) * mm, v(-37.32, 53.15) * mm, v(-37.3, 53.13) * mm, v(-37.3, 53.12) * mm, v(-37.29, 53.1) * mm, v(-37.28, 53.08) * mm, v(-37.27, 53.07) * mm, v(-37.26, 53.05) * mm, v(-37.24, 53.04) * mm, v(-37.23, 53.03) * mm, v(-37.21, 53) * mm, v(-37.2, 53) * mm, v(-37.19, 52.98) * mm, v(-37.16, 52.96) * mm, v(-37.15, 52.95) * mm, v(-37.13, 52.94) * mm, v(-37.11, 52.92) * mm, v(-37.1, 52.91) * mm, v(-37.07, 52.9) * mm, v(-37.04, 52.9) * mm, v(-37.02, 52.9) * mm, v(-36.99, 52.88) * mm, v(-36.96, 52.88) * mm, v(-36.92, 52.88) * mm, v(-36.9, 52.87) * mm, v(-36.87, 52.87) * mm, v(-36.84, 52.87) * mm, v(-36.8, 52.88) * mm, v(-36.78, 52.88) * mm, v(-36.76, 52.89) * mm, v(-36.73, 52.9) * mm, v(-36.69, 52.9) * mm, v(-36.66, 52.9) * mm, v(-36.66, 52.9) * mm, v(-36.64, 52.92) * mm, v(-36.62, 52.93) * mm, v(-36.6, 52.95) * mm, v(-36.57, 52.96) * mm, v(-36.53, 52.98) * mm, v(-36.5, 53) * mm, v(-36.47, 53.03) * mm, v(-36.46, 53.03) * mm, v(-36.43, 53.06) * mm, v(-36.42, 53.07) * mm, v(-36.4, 53.09) * mm, v(-36.39, 53.1) * mm, v(-36.37, 53.12) * mm, v(-36.35, 53.14) * mm, v(-36.34, 53.15) * mm, v(-36.33, 53.17) * mm, v(-36.32, 53.18) * mm, v(-36.3, 53.2) * mm, v(-36.3, 53.21) * mm, v(-36.28, 53.22) * mm, v(-36.27, 53.23) * mm, v(-36.26, 53.26) * mm], "startDerivative": vector(1.94, 1.4) * mm, "endDerivative": vector(1, 1.6) * mm});
            skFitSpline(sketch, "E42", {"points": [v(-36.26, 53.26) * mm, v(-36.24, 53.28) * mm, v(-36.24, 53.3) * mm, v(-36.21, 53.34) * mm, v(-36.2, 53.37) * mm, v(-36.19, 53.4) * mm, v(-36.18, 53.46) * mm, v(-36.15, 53.51) * mm, v(-36.14, 53.57) * mm, v(-36.14, 53.65) * mm, v(-36.14, 53.68) * mm, v(-36.14, 53.78) * mm, v(-36.15, 53.85) * mm, v(-36.15, 53.88) * mm, v(-36.17, 53.92) * mm, v(-36.18, 53.95) * mm, v(-36.2, 53.97) * mm, v(-36.21, 54) * mm, v(-36.24, 54.03) * mm, v(-36.26, 54.05) * mm, v(-36.28, 54.08) * mm, v(-36.31, 54.11) * mm, v(-36.33, 54.14) * mm, v(-36.35, 54.15) * mm, v(-36.39, 54.17) * mm, v(-36.42, 54.19) * mm, v(-36.47, 54.2) * mm, v(-36.5, 54.2) * mm, v(-36.54, 54.2) * mm, v(-36.58, 54.2) * mm, v(-36.62, 54.2) * mm, v(-36.68, 54.2) * mm, v(-36.71, 54.19) * mm, v(-36.76, 54.17) * mm, v(-36.83, 54.14) * mm, v(-36.86, 54.12) * mm, v(-36.9, 54.08) * mm, v(-36.93, 54.07) * mm, v(-36.95, 54.05) * mm, v(-36.98, 54.04) * mm, v(-36.99, 54.02) * mm, v(-37.02, 53.98) * mm, v(-37.04, 53.96) * mm, v(-37.09, 53.92) * mm, v(-37.12, 53.88) * mm, v(-37.14, 53.83) * mm, v(-37.17, 53.8) * mm, v(-37.18, 53.77) * mm, v(-37.2, 53.75) * mm, v(-37.23, 53.72) * mm, v(-37.25, 53.68) * mm, v(-37.28, 53.65) * mm, v(-37.3, 53.6) * mm, v(-37.33, 53.57) * mm, v(-37.35, 53.54) * mm, v(-37.37, 53.52) * mm, v(-37.4, 53.5) * mm, v(-37.42, 53.44) * mm, v(-37.44, 53.42) * mm, v(-37.47, 53.38) * mm, v(-37.5, 53.35) * mm, v(-37.51, 53.33) * mm, v(-37.53, 53.31) * mm, v(-37.56, 53.29) * mm, v(-37.6, 53.26) * mm, v(-37.63, 53.24) * mm, v(-37.65, 53.21) * mm, v(-37.68, 53.2) * mm, v(-37.7, 53.18) * mm, v(-37.71, 53.17) * mm, v(-37.73, 53.16) * mm, v(-37.76, 53.15) * mm, v(-37.77, 53.14) * mm, v(-37.79, 53.14) * mm, v(-37.81, 53.13) * mm, v(-37.84, 53.13) * mm, v(-37.85, 53.13) * mm, v(-37.88, 53.13) * mm, v(-37.9, 53.12) * mm, v(-37.9, 53.13) * mm, v(-37.92, 53.13) * mm, v(-37.94, 53.14) * mm, v(-37.94, 53.14) * mm, v(-37.95, 53.15) * mm], "startDerivative": vector(1.57, 2.59) * mm, "endDerivative": vector(-1.42, 0.87) * mm});
            skFitSpline(sketch, "E43", {"points": [v(-37.95, 53.15) * mm, v(-37.97, 53.17) * mm, v(-38, 53.18) * mm, v(-38.01, 53.2) * mm, v(-38.02, 53.22) * mm, v(-38.03, 53.26) * mm, v(-38.04, 53.28) * mm, v(-38.04, 53.33) * mm, v(-38.04, 53.37) * mm, v(-38.04, 53.4) * mm, v(-38.04, 53.41) * mm, v(-38.03, 53.45) * mm, v(-38.03, 53.5) * mm, v(-38.03, 53.53) * mm, v(-38.02, 53.55) * mm, v(-38.02, 53.58) * mm, v(-38.02, 53.62) * mm, v(-38, 53.67) * mm, v(-38, 53.7) * mm, v(-37.98, 53.74) * mm, v(-37.95, 53.78) * mm, v(-37.94, 53.8) * mm, v(-37.93, 53.82) * mm, v(-37.91, 53.86) * mm, v(-37.9, 53.88) * mm, v(-37.88, 53.9) * mm, v(-37.87, 53.92) * mm, v(-37.86, 53.95) * mm, v(-37.83, 53.97) * mm, v(-37.81, 53.99) * mm, v(-37.8, 54) * mm, v(-37.76, 54.02) * mm, v(-37.74, 54.04) * mm, v(-37.7, 54.05) * mm, v(-37.7, 54.05) * mm, v(-37.66, 54.04) * mm, v(-37.64, 54.04) * mm, v(-37.62, 54.04) * mm, v(-37.6, 54.03) * mm, v(-37.59, 54.02) * mm, v(-37.58, 54.01) * mm, v(-37.57, 54) * mm, v(-37.56, 53.99) * mm, v(-37.56, 53.97) * mm, v(-37.57, 53.96) * mm, v(-37.6, 53.96) * mm, v(-37.62, 53.96) * mm, v(-37.64, 53.96) * mm, v(-37.66, 53.96) * mm, v(-37.66, 53.94) * mm, v(-37.67, 53.94) * mm, v(-37.68, 53.92) * mm, v(-37.69, 53.9) * mm, v(-37.7, 53.9) * mm, v(-37.7, 53.88) * mm, v(-37.7, 53.86) * mm, v(-37.7, 53.84) * mm, v(-37.7, 53.8) * mm, v(-37.69, 53.79) * mm, v(-37.68, 53.77) * mm, v(-37.67, 53.75) * mm, v(-37.67, 53.74) * mm, v(-37.65, 53.72) * mm, v(-37.65, 53.72) * mm, v(-37.64, 53.7) * mm, v(-37.62, 53.7) * mm, v(-37.6, 53.7) * mm, v(-37.56, 53.7) * mm, v(-37.53, 53.7) * mm, v(-37.5, 53.7) * mm, v(-37.47, 53.7) * mm, v(-37.45, 53.7) * mm, v(-37.42, 53.72) * mm, v(-37.4, 53.74) * mm, v(-37.38, 53.76) * mm, v(-37.35, 53.8) * mm, v(-37.35, 53.87) * mm], "startDerivative": vector(-1.4, 1.59) * mm, "endDerivative": vector(-0.24, 2.25) * mm});
            skFitSpline(sketch, "E44", {"points": [v(-37.35, 53.87) * mm, v(-37.35, 53.88) * mm, v(-37.35, 53.92) * mm, v(-37.35, 53.96) * mm, v(-37.37, 53.98) * mm, v(-37.37, 54) * mm, v(-37.38, 54.04) * mm, v(-37.4, 54.06) * mm, v(-37.41, 54.07) * mm, v(-37.44, 54.1) * mm, v(-37.48, 54.13) * mm, v(-37.5, 54.14) * mm, v(-37.5, 54.15) * mm, v(-37.53, 54.17) * mm, v(-37.56, 54.18) * mm, v(-37.58, 54.2) * mm, v(-37.62, 54.2) * mm, v(-37.65, 54.2) * mm, v(-37.67, 54.2) * mm, v(-37.71, 54.21) * mm, v(-37.75, 54.2) * mm, v(-37.76, 54.2) * mm, v(-37.79, 54.2) * mm, v(-37.83, 54.2) * mm, v(-37.86, 54.2) * mm, v(-37.9, 54.18) * mm, v(-37.92, 54.16) * mm, v(-37.95, 54.15) * mm, v(-37.96, 54.13) * mm, v(-37.99, 54.12) * mm, v(-38.02, 54.1) * mm, v(-38.03, 54.08) * mm, v(-38.06, 54.07) * mm, v(-38.08, 54.05) * mm, v(-38.09, 54.04) * mm, v(-38.1, 54.02) * mm, v(-38.12, 54) * mm, v(-38.13, 54) * mm, v(-38.15, 53.98) * mm, v(-38.17, 53.96) * mm, v(-38.18, 53.95) * mm, v(-38.2, 53.93) * mm, v(-38.22, 53.91) * mm, v(-38.23, 53.9) * mm, v(-38.26, 53.88) * mm, v(-38.28, 53.87) * mm, v(-38.3, 53.84) * mm, v(-38.31, 53.83) * mm, v(-38.33, 53.81) * mm, v(-38.34, 53.8) * mm, v(-38.36, 53.78) * mm, v(-38.36, 53.77) * mm, v(-38.38, 53.74) * mm, v(-38.4, 53.73) * mm, v(-38.42, 53.7) * mm, v(-38.44, 53.7) * mm, v(-38.46, 53.66) * mm, v(-38.47, 53.64) * mm, v(-38.49, 53.63) * mm, v(-38.5, 53.6) * mm, v(-38.52, 53.59) * mm, v(-38.54, 53.57) * mm, v(-38.56, 53.56) * mm, v(-38.58, 53.53) * mm, v(-38.6, 53.52) * mm, v(-38.61, 53.51) * mm, v(-38.62, 53.51) * mm, v(-38.64, 53.52) * mm, v(-38.65, 53.52) * mm, v(-38.65, 53.53) * mm, v(-38.66, 53.55) * mm, v(-38.66, 53.57) * mm, v(-38.66, 53.6) * mm, v(-38.65, 53.61) * mm, v(-38.65, 53.65) * mm, v(-38.64, 53.67) * mm, v(-38.64, 53.7) * mm, v(-38.63, 53.71) * mm, v(-38.63, 53.73) * mm, v(-38.63, 53.75) * mm, v(-38.63, 53.77) * mm, v(-38.63, 53.8) * mm, v(-38.63, 53.8) * mm, v(-38.63, 53.84) * mm, v(-38.64, 53.87) * mm, v(-38.64, 53.87) * mm, v(-38.64, 53.88) * mm, v(-38.65, 53.9) * mm, v(-38.65, 53.92) * mm, v(-38.65, 53.93) * mm, v(-38.65, 53.95) * mm, v(-38.66, 53.96) * mm, v(-38.67, 53.97) * mm, v(-38.67, 53.98) * mm, v(-38.68, 54) * mm, v(-38.7, 54.03) * mm, v(-38.7, 54.05) * mm, v(-38.71, 54.05) * mm, v(-38.73, 54.07) * mm], "startDerivative": vector(0.04, 2.41) * mm, "endDerivative": vector(-1.2, 1.48) * mm});
            skFitSpline(sketch, "E45", {"points": [v(-38.73, 54.07) * mm, v(-38.75, 54.1) * mm, v(-38.77, 54.12) * mm, v(-38.8, 54.14) * mm, v(-38.84, 54.16) * mm, v(-38.86, 54.17) * mm, v(-38.9, 54.17) * mm, v(-38.91, 54.18) * mm, v(-38.98, 54.19) * mm, v(-39.02, 54.2) * mm, v(-39.05, 54.19) * mm, v(-39.1, 54.18) * mm, v(-39.16, 54.18) * mm, v(-39.16, 54.17) * mm, v(-39.18, 54.16) * mm, v(-39.21, 54.16) * mm, v(-39.22, 54.15) * mm, v(-39.23, 54.14) * mm, v(-39.24, 54.13) * mm, v(-39.26, 54.12) * mm, v(-39.27, 54.11) * mm, v(-39.3, 54.11) * mm, v(-39.3, 54.12) * mm], "startDerivative": vector(-0.52, 0.67) * mm, "endDerivative": vector(-0.05, 0.25) * mm});
            skFitSpline(sketch, "E46", {"points": [v(-39.3, 54.14) * mm, v(-39.3, 54.17) * mm, v(-39.3, 54.19) * mm, v(-39.33, 54.19) * mm, v(-39.38, 54.19) * mm, v(-39.42, 54.2) * mm, v(-39.5, 54.19) * mm, v(-39.52, 54.2) * mm, v(-39.54, 54.2) * mm, v(-39.57, 54.2) * mm, v(-39.63, 54.2) * mm, v(-39.69, 54.2) * mm, v(-39.71, 54.2) * mm, v(-39.77, 54.2) * mm, v(-39.8, 54.2) * mm, v(-39.85, 54.2) * mm, v(-39.86, 54.2) * mm, v(-39.87, 54.18) * mm, v(-39.87, 54.16) * mm, v(-39.87, 54.14) * mm, v(-39.88, 54.11) * mm, v(-39.88, 54.09) * mm, v(-39.88, 54.07) * mm, v(-39.88, 54.07) * mm, v(-39.87, 54.07) * mm, v(-39.85, 54.07) * mm, v(-39.82, 54.07) * mm, v(-39.8, 54.07) * mm, v(-39.77, 54.07) * mm, v(-39.76, 54.05) * mm, v(-39.76, 54.02) * mm, v(-39.75, 54.01) * mm, v(-39.77, 54) * mm, v(-39.77, 53.99) * mm, v(-39.78, 53.96) * mm, v(-39.79, 53.94) * mm, v(-39.8, 53.91) * mm, v(-39.8, 53.9) * mm, v(-39.84, 53.84) * mm], "startDerivative": vector(-0.08, 1.05) * mm, "endDerivative": vector(-1.3, -1.4) * mm});
            skLineSegment(sketch, "E47", {"start": v(-39.3, 54.12) * mm, "end": v(-39.3, 54.14) * mm});
            skFitSpline(sketch, "E48", {"points": [v(-39.84, 53.84) * mm, v(-39.86, 53.8) * mm, v(-39.88, 53.77) * mm, v(-39.9, 53.75) * mm, v(-39.9, 53.73) * mm, v(-39.92, 53.7) * mm, v(-39.94, 53.69) * mm, v(-39.95, 53.67) * mm, v(-39.96, 53.66) * mm, v(-39.98, 53.62) * mm, v(-40, 53.61) * mm, v(-40, 53.6) * mm, v(-40.02, 53.59) * mm, v(-40.03, 53.57) * mm, v(-40.04, 53.56) * mm, v(-40.06, 53.54) * mm, v(-40.07, 53.54) * mm, v(-40.07, 53.54) * mm, v(-40.08, 53.55) * mm, v(-40.1, 53.57) * mm, v(-40.1, 53.61) * mm, v(-40.09, 53.63) * mm, v(-40.09, 53.65) * mm, v(-40.08, 53.68) * mm, v(-40.08, 53.7) * mm, v(-40.08, 53.73) * mm, v(-40.08, 53.74) * mm, v(-40.09, 53.77) * mm, v(-40.1, 53.8) * mm, v(-40.1, 53.83) * mm, v(-40.1, 53.88) * mm, v(-40.1, 53.91) * mm, v(-40.11, 53.94) * mm, v(-40.11, 53.96) * mm, v(-40.12, 53.98) * mm, v(-40.13, 54) * mm, v(-40.14, 54.04) * mm, v(-40.15, 54.06) * mm, v(-40.17, 54.08) * mm, v(-40.18, 54.1) * mm, v(-40.2, 54.13) * mm, v(-40.22, 54.14) * mm, v(-40.23, 54.15) * mm, v(-40.25, 54.16) * mm, v(-40.27, 54.19) * mm, v(-40.3, 54.2) * mm, v(-40.31, 54.2) * mm, v(-40.34, 54.22) * mm, v(-40.36, 54.23) * mm, v(-40.4, 54.23) * mm, v(-40.42, 54.23) * mm, v(-40.44, 54.23) * mm, v(-40.48, 54.23) * mm, v(-40.5, 54.23) * mm, v(-40.53, 54.23) * mm, v(-40.55, 54.23) * mm, v(-40.58, 54.22) * mm, v(-40.6, 54.21) * mm, v(-40.63, 54.2) * mm, v(-40.65, 54.2) * mm, v(-40.66, 54.2) * mm, v(-40.7, 54.18) * mm, v(-40.7, 54.17) * mm, v(-40.73, 54.16) * mm, v(-40.75, 54.14) * mm, v(-40.78, 54.13) * mm, v(-40.81, 54.1) * mm, v(-40.82, 54.08) * mm, v(-40.84, 54.06) * mm, v(-40.86, 54.05) * mm, v(-40.9, 54.02) * mm, v(-40.92, 54.01) * mm, v(-40.95, 53.99) * mm, v(-40.96, 53.97) * mm, v(-40.97, 53.95) * mm, v(-41, 53.93) * mm], "startDerivative": vector(-1.1, -2.03) * mm, "endDerivative": vector(-1.67, -1.4) * mm});
            skFitSpline(sketch, "E49", {"points": [v(-41, 53.93) * mm, v(-41.03, 53.88) * mm, v(-41.04, 53.86) * mm, v(-41.07, 53.84) * mm, v(-41.1, 53.8) * mm, v(-41.11, 53.78) * mm, v(-41.15, 53.74) * mm, v(-41.17, 53.7) * mm, v(-41.18, 53.67) * mm, v(-41.2, 53.62) * mm, v(-41.23, 53.6) * mm, v(-41.24, 53.57) * mm, v(-41.27, 53.55) * mm, v(-41.28, 53.53) * mm, v(-41.3, 53.5) * mm, v(-41.3, 53.47) * mm, v(-41.32, 53.44) * mm, v(-41.35, 53.43) * mm, v(-41.37, 53.4) * mm, v(-41.38, 53.39) * mm, v(-41.39, 53.37) * mm, v(-41.4, 53.35) * mm, v(-41.43, 53.31) * mm, v(-41.43, 53.31) * mm, v(-41.44, 53.3) * mm, v(-41.46, 53.27) * mm], "startDerivative": vector(-0.9, -0.8) * mm, "endDerivative": vector(-0.25, -0.4) * mm});
            skFitSpline(sketch, "E50", {"points": [v(-41.46, 53.27) * mm, v(-41.49, 53.25) * mm, v(-41.5, 53.23) * mm, v(-41.52, 53.22) * mm, v(-41.54, 53.2) * mm, v(-41.57, 53.19) * mm, v(-41.6, 53.18) * mm, v(-41.62, 53.17) * mm, v(-41.63, 53.16) * mm, v(-41.65, 53.15) * mm, v(-41.66, 53.14) * mm, v(-41.7, 53.13) * mm, v(-41.73, 53.13) * mm, v(-41.76, 53.14) * mm, v(-41.77, 53.14) * mm, v(-41.8, 53.14) * mm, v(-41.8, 53.14) * mm, v(-41.83, 53.14) * mm, v(-41.85, 53.16) * mm, v(-41.87, 53.16) * mm, v(-41.9, 53.18) * mm, v(-41.9, 53.19) * mm, v(-41.92, 53.23) * mm, v(-41.94, 53.26) * mm, v(-41.95, 53.3) * mm, v(-41.95, 53.3) * mm, v(-41.96, 53.33) * mm, v(-41.96, 53.36) * mm, v(-41.97, 53.37) * mm, v(-41.97, 53.39) * mm, v(-41.98, 53.42) * mm, v(-41.98, 53.45) * mm, v(-41.98, 53.49) * mm, v(-41.98, 53.54) * mm, v(-41.98, 53.57) * mm, v(-41.97, 53.6) * mm, v(-41.98, 53.64) * mm, v(-41.97, 53.68) * mm, v(-41.97, 53.7) * mm, v(-41.96, 53.73) * mm, v(-41.96, 53.76) * mm, v(-41.95, 53.8) * mm, v(-41.94, 53.83) * mm, v(-41.92, 53.87) * mm, v(-41.9, 53.95) * mm, v(-41.9, 54) * mm, v(-41.88, 54.06) * mm, v(-41.86, 54.09) * mm, v(-41.83, 54.15) * mm, v(-41.83, 54.16) * mm, v(-41.8, 54.2) * mm, v(-41.77, 54.24) * mm, v(-41.76, 54.27) * mm, v(-41.74, 54.3) * mm, v(-41.73, 54.31) * mm, v(-41.71, 54.33) * mm, v(-41.7, 54.37) * mm, v(-41.7, 54.38) * mm, v(-41.67, 54.4) * mm, v(-41.65, 54.42) * mm, v(-41.62, 54.45) * mm, v(-41.6, 54.47) * mm, v(-41.6, 54.5) * mm, v(-41.58, 54.5) * mm, v(-41.56, 54.52) * mm, v(-41.53, 54.54) * mm, v(-41.51, 54.55) * mm, v(-41.5, 54.57) * mm, v(-41.5, 54.58) * mm, v(-41.48, 54.6) * mm, v(-41.46, 54.6) * mm, v(-41.46, 54.63) * mm, v(-41.43, 54.63) * mm, v(-41.42, 54.63) * mm, v(-41.38, 54.63) * mm, v(-41.38, 54.63) * mm, v(-41.34, 54.63) * mm, v(-41.34, 54.63) * mm, v(-41.31, 54.62) * mm, v(-41.3, 54.61) * mm, v(-41.28, 54.6) * mm, v(-41.27, 54.59) * mm, v(-41.25, 54.57) * mm, v(-41.24, 54.55) * mm, v(-41.23, 54.53) * mm, v(-41.22, 54.5) * mm, v(-41.2, 54.48) * mm, v(-41.2, 54.46) * mm, v(-41.2, 54.44) * mm, v(-41.19, 54.4) * mm, v(-41.17, 54.37) * mm, v(-41.16, 54.35) * mm, v(-41.16, 54.32) * mm, v(-41.16, 54.29) * mm, v(-41.16, 54.27) * mm, v(-41.16, 54.24) * mm, v(-41.16, 54.22) * mm, v(-41.16, 54.2) * mm, v(-41.15, 54.19) * mm], "startDerivative": vector(-2.37, -1.96) * mm, "endDerivative": vector(1.15, 0.05) * mm});
            skFitSpline(sketch, "E51", {"points": [v(-41.15, 54.19) * mm, v(-41.13, 54.17) * mm, v(-41.09, 54.17) * mm, v(-41.07, 54.17) * mm, v(-41.05, 54.17) * mm, v(-41.01, 54.18) * mm, v(-41, 54.19) * mm, v(-40.98, 54.21) * mm, v(-40.98, 54.24) * mm, v(-40.98, 54.27) * mm, v(-40.97, 54.32) * mm, v(-40.97, 54.35) * mm, v(-40.96, 54.37) * mm, v(-40.95, 54.4) * mm, v(-40.94, 54.44) * mm, v(-40.94, 54.46) * mm, v(-40.93, 54.5) * mm, v(-40.91, 54.54) * mm, v(-40.9, 54.57) * mm, v(-40.9, 54.6) * mm, v(-40.89, 54.65) * mm, v(-40.88, 54.66) * mm, v(-40.87, 54.7) * mm, v(-40.85, 54.73) * mm, v(-40.84, 54.74) * mm, v(-40.85, 54.78) * mm, v(-40.85, 54.8) * mm, v(-40.9, 54.8) * mm, v(-40.92, 54.8) * mm, v(-40.97, 54.8) * mm, v(-41, 54.8) * mm, v(-41.01, 54.79) * mm, v(-41.02, 54.77) * mm, v(-41.03, 54.73) * mm, v(-41.04, 54.72) * mm, v(-41.05, 54.72) * mm, v(-41.07, 54.71) * mm, v(-41.1, 54.71) * mm, v(-41.12, 54.73) * mm, v(-41.15, 54.75) * mm, v(-41.15, 54.76) * mm, v(-41.2, 54.79) * mm, v(-41.22, 54.8) * mm, v(-41.25, 54.82) * mm, v(-41.29, 54.82) * mm, v(-41.32, 54.84) * mm, v(-41.37, 54.84) * mm, v(-41.4, 54.84) * mm, v(-41.43, 54.85) * mm, v(-41.48, 54.85) * mm, v(-41.5, 54.85) * mm, v(-41.54, 54.84) * mm, v(-41.58, 54.84) * mm, v(-41.63, 54.82) * mm, v(-41.67, 54.81) * mm, v(-41.7, 54.8) * mm, v(-41.74, 54.79) * mm, v(-41.8, 54.75) * mm, v(-41.84, 54.72) * mm, v(-41.85, 54.72) * mm, v(-41.87, 54.71) * mm, v(-41.9, 54.69) * mm, v(-41.91, 54.68) * mm, v(-41.93, 54.65) * mm, v(-41.94, 54.64) * mm, v(-41.96, 54.63) * mm, v(-41.99, 54.6) * mm], "startDerivative": vector(1.2, -1.4) * mm, "endDerivative": vector(-2.24, -0.4) * mm});
            skFitSpline(sketch, "E52", {"points": [v(-41.99, 54.6) * mm, v(-42.01, 54.58) * mm, v(-42.03, 54.56) * mm, v(-42.04, 54.55) * mm, v(-42.06, 54.54) * mm, v(-42.07, 54.51) * mm, v(-42.1, 54.5) * mm, v(-42.1, 54.49) * mm, v(-42.1, 54.47) * mm, v(-42.13, 54.45) * mm, v(-42.16, 54.42) * mm, v(-42.18, 54.4) * mm, v(-42.2, 54.36) * mm, v(-42.24, 54.31) * mm, v(-42.25, 54.27) * mm, v(-42.27, 54.23) * mm, v(-42.29, 54.2) * mm, v(-42.3, 54.17) * mm, v(-42.3, 54.14) * mm, v(-42.31, 54.12) * mm, v(-42.33, 54.08) * mm, v(-42.34, 54.06) * mm, v(-42.36, 54.03) * mm, v(-42.37, 54) * mm, v(-42.38, 53.98) * mm, v(-42.38, 53.95) * mm, v(-42.38, 53.9) * mm, v(-42.4, 53.9) * mm, v(-42.4, 53.87) * mm, v(-42.4, 53.85) * mm, v(-42.4, 53.84) * mm, v(-42.4, 53.8) * mm, v(-42.41, 53.77) * mm, v(-42.42, 53.74) * mm, v(-42.43, 53.67) * mm, v(-42.42, 53.64) * mm, v(-42.43, 53.6) * mm, v(-42.43, 53.57) * mm, v(-42.43, 53.5) * mm, v(-42.43, 53.47) * mm, v(-42.43, 53.42) * mm, v(-42.42, 53.37) * mm, v(-42.4, 53.32) * mm, v(-42.38, 53.27) * mm, v(-42.36, 53.23) * mm, v(-42.35, 53.18) * mm, v(-42.32, 53.13) * mm, v(-42.3, 53.1) * mm, v(-42.28, 53.07) * mm, v(-42.28, 53.07) * mm, v(-42.25, 53.05) * mm, v(-42.23, 53.02) * mm, v(-42.2, 53) * mm], "startDerivative": vector(-1.39, -1.2) * mm, "endDerivative": vector(1.74, -1.1) * mm});
            skFitSpline(sketch, "E53", {"points": [v(-40.54, 54.05) * mm, v(-40.59, 54.03) * mm, v(-40.62, 54) * mm, v(-40.65, 53.97) * mm, v(-40.68, 53.94) * mm, v(-40.7, 53.9) * mm, v(-40.72, 53.86) * mm, v(-40.74, 53.83) * mm, v(-40.75, 53.8) * mm, v(-40.76, 53.76) * mm, v(-40.78, 53.73) * mm, v(-40.8, 53.7) * mm, v(-40.8, 53.64) * mm, v(-40.82, 53.62) * mm, v(-40.83, 53.58) * mm, v(-40.85, 53.53) * mm, v(-40.86, 53.5) * mm, v(-40.87, 53.46) * mm, v(-40.88, 53.44) * mm, v(-40.9, 53.39) * mm, v(-40.9, 53.33) * mm, v(-40.9, 53.27) * mm, v(-40.9, 53.23) * mm, v(-40.9, 53.16) * mm, v(-40.88, 53.14) * mm, v(-40.87, 53.12) * mm, v(-40.85, 53.08) * mm, v(-40.82, 53.06) * mm, v(-40.77, 53.05) * mm, v(-40.75, 53.04) * mm, v(-40.7, 53.05) * mm, v(-40.69, 53.05) * mm, v(-40.66, 53.06) * mm, v(-40.63, 53.08) * mm, v(-40.6, 53.1) * mm, v(-40.57, 53.14) * mm, v(-40.54, 53.17) * mm, v(-40.52, 53.2) * mm, v(-40.48, 53.25) * mm, v(-40.47, 53.29) * mm, v(-40.43, 53.34) * mm, v(-40.42, 53.39) * mm, v(-40.4, 53.43) * mm, v(-40.4, 53.46) * mm, v(-40.38, 53.51) * mm, v(-40.37, 53.56) * mm, v(-40.37, 53.6) * mm, v(-40.36, 53.66) * mm, v(-40.34, 53.73) * mm, v(-40.34, 53.77) * mm, v(-40.34, 53.83) * mm], "startDerivative": vector(-2.37, -0.75) * mm, "endDerivative": vector(0.2, 2.32) * mm});
            skFitSpline(sketch, "E54", {"points": [v(-40.34, 53.83) * mm, v(-40.34, 53.87) * mm, v(-40.34, 53.91) * mm, v(-40.36, 53.95) * mm, v(-40.37, 53.98) * mm, v(-40.4, 54) * mm, v(-40.43, 54.02) * mm, v(-40.45, 54.03) * mm, v(-40.47, 54.04) * mm, v(-40.51, 54.06) * mm, v(-40.54, 54.05) * mm], "startDerivative": vector(0, 0.37) * mm, "endDerivative": vector(-0.29, -0.12) * mm});
            skFitSpline(sketch, "E55", {"points": [v(-39.17, 54) * mm, v(-39.24, 54) * mm, v(-39.25, 53.99) * mm, v(-39.27, 53.98) * mm, v(-39.29, 53.96) * mm, v(-39.3, 53.95) * mm, v(-39.32, 53.94) * mm, v(-39.33, 53.92) * mm, v(-39.35, 53.9) * mm, v(-39.36, 53.88) * mm, v(-39.38, 53.86) * mm, v(-39.4, 53.83) * mm, v(-39.4, 53.81) * mm, v(-39.41, 53.77) * mm, v(-39.41, 53.73) * mm, v(-39.43, 53.72) * mm, v(-39.44, 53.7) * mm, v(-39.45, 53.68) * mm, v(-39.45, 53.67) * mm, v(-39.45, 53.64) * mm, v(-39.45, 53.62) * mm, v(-39.46, 53.6) * mm, v(-39.46, 53.58) * mm, v(-39.47, 53.55) * mm, v(-39.47, 53.54) * mm, v(-39.48, 53.51) * mm, v(-39.49, 53.49) * mm, v(-39.49, 53.46) * mm, v(-39.5, 53.43) * mm, v(-39.5, 53.4) * mm, v(-39.51, 53.39) * mm, v(-39.54, 53.36) * mm, v(-39.54, 53.33) * mm, v(-39.54, 53.32) * mm, v(-39.54, 53.3) * mm, v(-39.54, 53.26) * mm, v(-39.54, 53.25) * mm, v(-39.54, 53.22) * mm, v(-39.54, 53.2) * mm, v(-39.54, 53.19) * mm, v(-39.54, 53.17) * mm, v(-39.54, 53.15) * mm, v(-39.53, 53.14) * mm, v(-39.53, 53.13) * mm, v(-39.52, 53.1) * mm, v(-39.5, 53.1) * mm, v(-39.5, 53.09) * mm, v(-39.48, 53.09) * mm, v(-39.46, 53.09) * mm, v(-39.44, 53.09) * mm, v(-39.44, 53.09) * mm, v(-39.42, 53.08) * mm, v(-39.41, 53.08) * mm, v(-39.36, 53.08) * mm, v(-39.36, 53.08) * mm, v(-39.35, 53.08) * mm, v(-39.34, 53.08) * mm, v(-39.32, 53.1) * mm, v(-39.3, 53.1) * mm, v(-39.3, 53.11) * mm, v(-39.26, 53.13) * mm, v(-39.24, 53.14) * mm, v(-39.23, 53.15) * mm], "startDerivative": vector(-2.79, 0.4) * mm, "endDerivative": vector(0.58, 1.06) * mm});
            skFitSpline(sketch, "E56", {"points": [v(-39.23, 53.15) * mm, v(-39.22, 53.16) * mm, v(-39.2, 53.18) * mm, v(-39.2, 53.18) * mm, v(-39.2, 53.19) * mm, v(-39.2, 53.2) * mm, v(-39.18, 53.2) * mm, v(-39.18, 53.2) * mm, v(-39.17, 53.22) * mm, v(-39.16, 53.23) * mm, v(-39.16, 53.24) * mm, v(-39.16, 53.25) * mm, v(-39.15, 53.26) * mm, v(-39.15, 53.27) * mm, v(-39.15, 53.27) * mm, v(-39.15, 53.28) * mm, v(-39.14, 53.29) * mm, v(-39.13, 53.3) * mm, v(-39.13, 53.31) * mm, v(-39.12, 53.33) * mm, v(-39.12, 53.33) * mm, v(-39.12, 53.35) * mm, v(-39.11, 53.36) * mm, v(-39.11, 53.37) * mm, v(-39.1, 53.37) * mm, v(-39.1, 53.38) * mm, v(-39.1, 53.4) * mm, v(-39.1, 53.41) * mm, v(-39.09, 53.42) * mm, v(-39.09, 53.43) * mm, v(-39.08, 53.44) * mm, v(-39.08, 53.46) * mm, v(-39.07, 53.47) * mm, v(-39.07, 53.48) * mm, v(-39.07, 53.5) * mm, v(-39.07, 53.51) * mm, v(-39.07, 53.52) * mm, v(-39.07, 53.53) * mm, v(-39.07, 53.55) * mm, v(-39.06, 53.57) * mm, v(-39.06, 53.58) * mm, v(-39.05, 53.59) * mm, v(-39.05, 53.6) * mm, v(-39.05, 53.62) * mm, v(-39.04, 53.64) * mm, v(-39.04, 53.66) * mm, v(-39.03, 53.68) * mm, v(-39.03, 53.7) * mm, v(-39.03, 53.7) * mm, v(-39.03, 53.72) * mm, v(-39.03, 53.74) * mm, v(-39.03, 53.75) * mm, v(-39.03, 53.76) * mm, v(-39.03, 53.76) * mm, v(-39.03, 53.79) * mm, v(-39.03, 53.8) * mm, v(-39.03, 53.82) * mm, v(-39.03, 53.84) * mm, v(-39.03, 53.85) * mm, v(-39.03, 53.88) * mm, v(-39.03, 53.89) * mm, v(-39.04, 53.9) * mm, v(-39.04, 53.91) * mm, v(-39.05, 53.92) * mm, v(-39.05, 53.93) * mm, v(-39.06, 53.94) * mm, v(-39.06, 53.95) * mm, v(-39.06, 53.95) * mm, v(-39.06, 53.96) * mm, v(-39.06, 53.97) * mm, v(-39.07, 53.97) * mm, v(-39.08, 53.98) * mm, v(-39.09, 53.98) * mm, v(-39.1, 53.99) * mm, v(-39.1, 54) * mm, v(-39.12, 54) * mm, v(-39.12, 54) * mm, v(-39.13, 54) * mm, v(-39.14, 54) * mm, v(-39.15, 54) * mm, v(-39.16, 54) * mm, v(-39.17, 54) * mm], "startDerivative": vector(0.77, 0.67) * mm, "endDerivative": vector(-0.93, 0.16) * mm});
            skFitSpline(sketch, "E57", {"points": [v(-36.8, 53.84) * mm, v(-36.83, 53.8) * mm, v(-36.84, 53.77) * mm, v(-36.85, 53.75) * mm, v(-36.86, 53.73) * mm, v(-36.86, 53.7) * mm, v(-36.87, 53.69) * mm, v(-36.88, 53.66) * mm, v(-36.9, 53.64) * mm, v(-36.9, 53.62) * mm, v(-36.9, 53.6) * mm, v(-36.91, 53.55) * mm, v(-36.92, 53.52) * mm, v(-36.93, 53.5) * mm, v(-36.94, 53.46) * mm, v(-36.94, 53.42) * mm, v(-36.95, 53.4) * mm, v(-36.95, 53.37) * mm, v(-36.95, 53.35) * mm, v(-36.95, 53.32) * mm, v(-36.95, 53.3) * mm, v(-36.95, 53.27) * mm, v(-36.95, 53.25) * mm, v(-36.96, 53.23) * mm, v(-36.95, 53.22) * mm, v(-36.95, 53.2) * mm, v(-36.94, 53.18) * mm, v(-36.94, 53.15) * mm, v(-36.94, 53.14) * mm, v(-36.92, 53.13) * mm, v(-36.92, 53.12) * mm, v(-36.9, 53.1) * mm, v(-36.9, 53.1) * mm, v(-36.88, 53.1) * mm, v(-36.87, 53.08) * mm, v(-36.85, 53.08) * mm, v(-36.82, 53.08) * mm, v(-36.8, 53.07) * mm, v(-36.79, 53.08) * mm, v(-36.77, 53.08) * mm, v(-36.75, 53.08) * mm, v(-36.73, 53.08) * mm, v(-36.72, 53.09) * mm, v(-36.7, 53.1) * mm, v(-36.69, 53.12) * mm, v(-36.68, 53.12) * mm, v(-36.66, 53.13) * mm, v(-36.65, 53.14) * mm, v(-36.64, 53.15) * mm, v(-36.63, 53.17) * mm, v(-36.61, 53.18) * mm, v(-36.6, 53.2) * mm, v(-36.6, 53.2) * mm, v(-36.58, 53.23) * mm, v(-36.57, 53.25) * mm, v(-36.56, 53.27) * mm, v(-36.56, 53.28) * mm, v(-36.55, 53.3) * mm, v(-36.53, 53.33) * mm, v(-36.52, 53.36) * mm, v(-36.52, 53.39) * mm, v(-36.5, 53.41) * mm, v(-36.5, 53.44) * mm, v(-36.49, 53.46) * mm, v(-36.47, 53.49) * mm, v(-36.47, 53.5) * mm, v(-36.47, 53.53) * mm, v(-36.46, 53.58) * mm, v(-36.45, 53.61) * mm, v(-36.44, 53.65) * mm, v(-36.44, 53.7) * mm, v(-36.44, 53.71) * mm, v(-36.43, 53.75) * mm, v(-36.44, 53.78) * mm, v(-36.43, 53.8) * mm, v(-36.43, 53.84) * mm, v(-36.43, 53.86) * mm, v(-36.44, 53.9) * mm, v(-36.44, 53.92) * mm, v(-36.44, 53.94) * mm, v(-36.46, 53.96) * mm, v(-36.46, 53.98) * mm, v(-36.48, 54) * mm, v(-36.5, 54.02) * mm, v(-36.52, 54.03) * mm, v(-36.54, 54.04) * mm, v(-36.57, 54.05) * mm, v(-36.58, 54.05) * mm, v(-36.61, 54.05) * mm, v(-36.63, 54.04) * mm, v(-36.65, 54.03) * mm, v(-36.66, 54.02) * mm, v(-36.68, 54.01) * mm, v(-36.7, 54) * mm, v(-36.71, 53.98) * mm, v(-36.73, 53.97) * mm, v(-36.73, 53.95) * mm, v(-36.74, 53.93) * mm, v(-36.75, 53.92) * mm, v(-36.77, 53.9) * mm, v(-36.78, 53.88) * mm, v(-36.8, 53.87) * mm, v(-36.8, 53.84) * mm]});
            skSolve(sketch);
        }
        {
            var Q0;
            Q0 = qSketchRegion(id + "F4", true);
            extrude(context, id + "F5", {"entities" : qUnion([Q0]), "operationType" : NewBodyOperationType.REMOVE, "oppositeDirection" : true, "depth" : 0.1 * mm});
        }
        {
            var Q0;
            {var subQ0=sQuery(id+"F0.wireOp",EDGE,"E0.top");var subQ1=sQuery(id+"F0.wireOp",EDGE,"E0.left");var subQ2=sQuery(id+"F0.wireOp",EDGE,"E0.right");Q0=makeQuery(id+"F5.boolean.opBoolean","SPLIT",FACE,{"disambiguationData":[TD([makeQuery(id+"F1.opExtrude","SWEPT_FACE",FACE,{"disambiguationData":[OSD([subQ0])]})])],"derivedFrom":makeQuery(id+"F1.opExtrude","CAP_FACE",FACE,{"disambiguationData":[OSD([sQuery(id+"F0.wireOp",EDGE,"E0.bottom"),subQ0,subQ1,subQ2])],"isStart":false})});}
            var sketch = newSketch(context, id + "F6", { "sketchPlane" : qUnion([Q0])});
            skLineSegment(sketch, "E58.bottom", {"start": v(-36.64, -30.93) * mm, "end": v(-37.39, -30.93) * mm});
            skLineSegment(sketch, "E58.top", {"start": v(-36.64, -24.93) * mm, "end": v(-37.39, -24.93) * mm});
            skLineSegment(sketch, "E58.left", {"start": v(-36.64, -30.93) * mm, "end": v(-36.64, -24.93) * mm});
            skLineSegment(sketch, "E58.right", {"start": v(-37.39, -30.93) * mm, "end": v(-37.39, -24.93) * mm});
            skLineSegment(sketch, "E59.bottom", {"start": v(-48.44, -30.93) * mm, "end": v(-47.69, -30.93) * mm});
            skLineSegment(sketch, "E59.top", {"start": v(-48.44, -24.93) * mm, "end": v(-47.69, -24.93) * mm});
            skLineSegment(sketch, "E59.left", {"start": v(-48.44, -30.93) * mm, "end": v(-48.44, -24.93) * mm});
            skLineSegment(sketch, "E59.right", {"start": v(-47.69, -30.93) * mm, "end": v(-47.69, -24.93) * mm});
            skSolve(sketch);
        }
        {
            var Q0;
            Q0 = qSketchRegion(id + "F6", true);
            extrude(context, id + "F7", {"entities" : qUnion([Q0]), "operationType" : NewBodyOperationType.REMOVE, "oppositeDirection" : true, "depth" : 0.2 * mm});
        }
        {
            var Q0;
            {var subQ0=sQuery(id+"F0.wireOp",EDGE,"E0.top");var subQ1=sQuery(id+"F0.wireOp",EDGE,"E0.left");var subQ2=sQuery(id+"F0.wireOp",EDGE,"E0.right");Q0=makeQuery(id+"F5.boolean.opBoolean","SPLIT",FACE,{"disambiguationData":[TD([makeQuery(id+"F1.opExtrude","SWEPT_FACE",FACE,{"disambiguationData":[OSD([subQ0])]})])],"derivedFrom":makeQuery(id+"F1.opExtrude","CAP_FACE",FACE,{"disambiguationData":[OSD([sQuery(id+"F0.wireOp",EDGE,"E0.bottom"),subQ0,subQ1,subQ2])],"isStart":false})});}
            var sketch = newSketch(context, id + "F8", { "sketchPlane" : qUnion([Q0])});
            skLineSegment(sketch, "E60.bottom", {"start": v(-45.54, -6.93) * mm, "end": v(-39.54, -6.93) * mm});
            skLineSegment(sketch, "E60.top", {"start": v(-45.54, -18.93) * mm, "end": v(-39.54, -18.93) * mm});
            skLineSegment(sketch, "E60.left", {"start": v(-45.54, -6.93) * mm, "end": v(-45.54, -18.93) * mm});
            skLineSegment(sketch, "E60.right", {"start": v(-39.54, -6.93) * mm, "end": v(-39.54, -18.93) * mm});
            skSolve(sketch);
        }
        {
            var Q0;
            Q0 = qSketchRegion(id + "F8", true);
            extrude(context, id + "F9", {"entities" : qUnion([Q0]), "operationType" : NewBodyOperationType.REMOVE, "oppositeDirection" : true, "depth" : 0.1 * mm});
        }
        {
            var Q0;
            Q0=makeQuery(id+"F9.boolean.opBoolean","COPY",FACE,{"derivedFrom":makeQuery(id+"F9.opExtrude","CAP_FACE",FACE,{"disambiguationData":[OSD([sQuery(id+"F8.wireOp",EDGE,"E60.bottom"),sQuery(id+"F8.wireOp",EDGE,"E60.top"),sQuery(id+"F8.wireOp",EDGE,"E60.left"),sQuery(id+"F8.wireOp",EDGE,"E60.right")])],"isStart":false})});
            var sketch = newSketch(context, id + "F10", { "sketchPlane" : qUnion([Q0])});
            skCircle(sketch, "E61", {"center": v(-42.54, -16.73) * mm, "radius": 0.7 * mm});
            skCircle(sketch, "E62", {"center": v(-42.54, -14.53) * mm, "radius": 0.7 * mm});
            skCircle(sketch, "E63", {"center": v(-42.54, -11.33) * mm, "radius": 0.7 * mm});
            skCircle(sketch, "E64", {"center": v(-42.54, -9.13) * mm, "radius": 0.7 * mm});
            skSolve(sketch);
        }
        {
            var Q0;
            Q0 = qSketchRegion(id + "F10", true);
            extrude(context, id + "F11", {"entities" : qUnion([Q0]), "operationType" : NewBodyOperationType.REMOVE, "oppositeDirection" : true, "depth" : 0.1 * mm});
        }
    });
